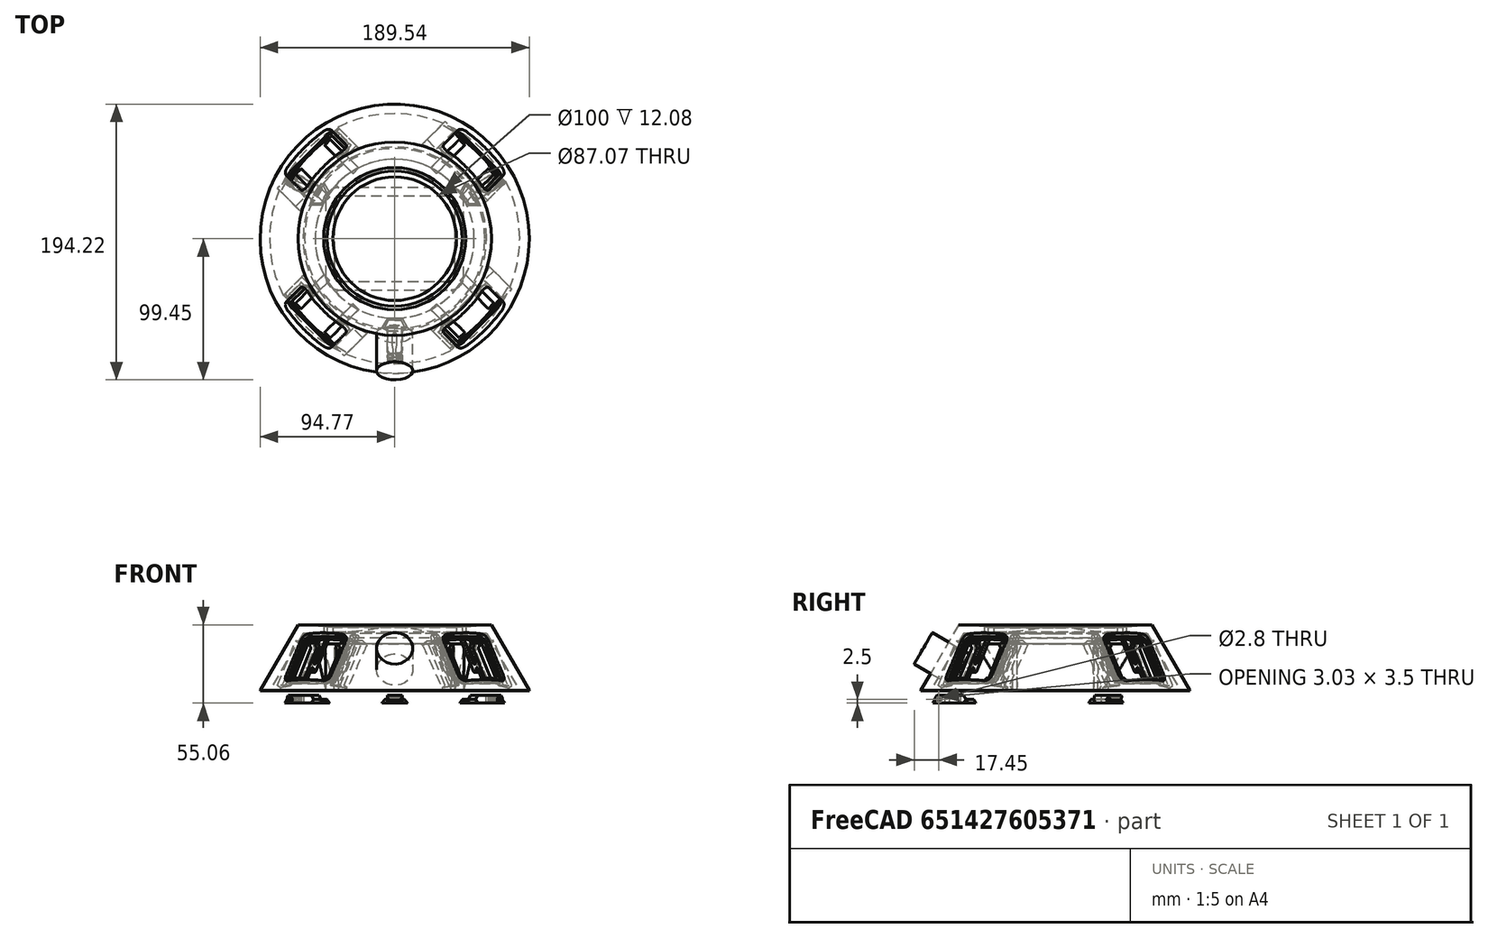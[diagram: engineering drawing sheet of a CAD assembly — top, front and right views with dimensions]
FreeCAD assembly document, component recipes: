
FREECAD ASSEMBLY — COMPONENT RECIPES ("case_v3_r2")

This assembly document has 20 components, labeled P0..P19 below (a component is one placed body or linked part). 20 of them carry a construction recipe — the FreeCAD feature program that regenerates the part from scratch, quoted from this document or its linked companion documents; the rest are supplied as boundary geometry only. No exploded tour is included for this assembly.
NOTE — this tour is split across 2 documents so each fits a 32k-token context. This is document 1: the component sections continue in the remaining 1 document, each repeating the header above.
COMPONENT P0 — recipe-attached ("BaseShape", modeled in this document).
Construction recipe (the document's own serialized feature program — sketch geometry with constraints, then the solid features built on it; lengths are millimeters unless a unit is written):

FEATURE [Sketcher::SketchObject] Sketch
  ArcFitTolerance = 1e-06
  AttachmentSupport = -> [XZ_Plane]
  FullyConstrained = true
  MakeInternals = false
  MapMode = 5
  Placement = pos=(0,0,0) rot=(1,0,0;1.5708rad)
  sketch-geometry (29):
    g0: LineSegment StartX=94.7691 StartY=0.4 StartZ=0 EndX=68.1243 EndY=46.55 EndZ=0
    g1: LineSegment [constr] StartX=50 StartY=45.0797 StartZ=0 EndX=50 EndY=0 EndZ=0
    g2: LineSegment [constr] StartX=50 StartY=0 StartZ=0 EndX=56 EndY=0 EndZ=0
    g3: LineSegment [constr] StartX=56 StartY=0 StartZ=0 EndX=56 EndY=33 EndZ=0
    g4: LineSegment StartX=63.55 StartY=40.55 StartZ=0 EndX=64.6602 EndY=40.55 EndZ=0
    g5: LineSegment StartX=64.6602 StartY=40.55 StartZ=0 EndX=88.0718 EndY=0 EndZ=0
    g6: LineSegment StartX=88.0718 StartY=0 StartZ=0 EndX=94.7681 EndY=0 EndZ=0
    g7: LineSegment StartX=50 StartY=45.0797 StartZ=0 EndX=68.1243 EndY=46.55 EndZ=0
    g8: LineSegment StartX=47.5346 StartY=44.8797 StartZ=0 EndX=43.5346 EndY=44.5552 EndZ=0
    g9: LineSegment StartX=47.5346 StartY=44.8797 StartZ=0 EndX=47.5346 EndY=37.3797 EndZ=0
    g10: LineSegment StartX=47.5346 StartY=37.3797 StartZ=0 EndX=0 EndY=37.3797 EndZ=0
    g11: LineSegment StartX=0 StartY=37.3797 StartZ=0 EndX=0 EndY=44.8797 EndZ=0
    g12: LineSegment StartX=43.5346 StartY=44.5552 StartZ=0 EndX=43.5346 EndY=41.3797 EndZ=0
    g13-g16: Circle [constr] x4 (B-spline internal-alignment scaffolding for g17; pole/knot coordinates omitted)
    g17: BSplineCurve PolesCount=4 KnotsCount=2 Degree=3 IsPeriodic=0
    g18: GeomPoint [constr] X=0 Y=44.8797 Z=0
    g19: GeomPoint [constr] X=43.5346 Y=41.3797 Z=0
    g20: GeomPoint [constr] X=95 Y=0 Z=0
    g21: ArcOfCircle [constr] CenterX=63.55 CenterY=33 CenterZ=0 NormalX=0 NormalY=0 NormalZ=1 AngleXU=0 Radius=7.55 StartAngle=1.5708 EndAngle=3.14159
    g22: GeomPoint [constr] X=56 Y=40.55 Z=0
    g23: LineSegment StartX=63.55 StartY=40.55 StartZ=0 EndX=56 EndY=33 EndZ=0
    g24: GeomPoint [constr] X=95 Y=0 Z=0
    g25: LineSegment StartX=94.7681 StartY=0 StartZ=0 EndX=94.7681 EndY=0.4 EndZ=0
    g26: LineSegment StartX=94.7691 StartY=0.4 StartZ=0 EndX=94.7681 EndY=0.4 EndZ=0
    g27: LineSegment StartX=56 StartY=33 StartZ=0 EndX=50 EndY=33 EndZ=0
    g28: LineSegment StartX=50 StartY=45.0797 StartZ=0 EndX=50 EndY=33 EndZ=0
  constraints (73):
    c: PointOnObject(g20,g-1)
    c: PointOnObject(g1,g-1)
    c: Coincident(g1,g2)
    c: PointOnObject(g2,g-1)
    c: Coincident(g2,g3)
    c: Horizontal(g4)
    c: Coincident(g4,g5)
    c: PointOnObject(g5,g-1)
    c: Coincident(g5,g6)
    c: DistanceX(g1) = 50
    c: Angle(g4,g5) = 2.0944
    c: Parallel(g5,g0)
    c: Distance(g20,g5) = 6
    c: Parallel(g3,g1)
    c: Distance(g1,g3) = 6
    c: Distance(g0,g4) = 6
    c: Vertical(g1)
    c: DistanceX(g20) = 95
    c: Coincident(g7,g1)
    c: Coincident(g7,g0)
    c: Distance(g22,g7) = 5
    c: Tangent(g8,g7)
    c: Coincident(g8,g9)
    c: Vertical(g9)
    c: Coincident(g9,g10)
    c: Horizontal(g10)
    c: Coincident(g10,g11)
    c: PointOnObject(g11,g-2)
    c: Vertical(g11)
    c: DistanceX(g8,g8) = 4
    c: Coincident(g12,g8)
    c: Vertical(g12)
    c: Weight(g13) = 1
    c: Equal(g13,g14)
    c: Equal(g13,g15)
    c: Equal(g13,g16)
    c: InternalAlignment(g13-g16 -> g17) x4
    c: InternalAlignment(g18,g17)
    c: InternalAlignment(g19,g17)
    c: Coincident(g17,g12)
    c: Coincident(g17,g11)
    c: Horizontal(g14,g11)
    c: Horizontal(g12,g15)
    c: DistanceY(g12,g11) = 3.5
    c: DistanceY(g10,g12) = 4
    c: Horizontal(g11,g8)
    c: Vertical(g15,g14)
    c: PointOnObject(g20,g0)
    c: PointOnObject(g20,g6)
    c: PointOnObject(g22,g3)
    c: PointOnObject(g22,g4)
    c: Tangent(g3,g21) = 1.5708
    c: Tangent(g4,g21) = 1.5708
    c: Coincident(g23,g3)
    c: Coincident(g23,g4)
    c: DistanceY(g0) = 46.55
    c: DistanceY(g8,g1) = 0.2
    c: DistanceY(g3) = 33
    c: PointOnObject(g24,g6)
    c: PointOnObject(g24,g0)
    c: Coincident(g25,g6)
    c: Vertical(g25)
    c: Coincident(g26,g0)
    c: Coincident(g26,g25)
    c: Horizontal(g26)
    c: DistanceY(g25,g25) = 0.4
    c: DistanceX(g26,g26) = 0.001
    c: DistanceX(g14) = 16
    c: Coincident(g27,g3)
    c: PointOnObject(g27,g1)
    c: Horizontal(g27)
    c: Coincident(g28,g1)
    c: Coincident(g28,g27)
FEATURE [PartDesign::Revolution] Revolution
  Angle = 360
  Angle2 = 60
  Axis = (0,2e-16,1)
  Base = (0,0,0)
  Placement = pos=(0,0,0) rot=(1,0,0;1.5708rad)
  Profile = -> Sketch
  ReferenceAxis = -> Sketch [V_Axis]
  Refine = true
  Suppressed = false
  Type = 0
FEATURE [PartDesign::SubShapeBinder] Binder012
  BindCopyOnChange = 0
  BindMode = 0
  ClaimChildren = false
  Context = -> Body [Binder012.]
  Fuse = false
  MakeFace = true
  OffsetFill = false
  OffsetIntersection = false
  OffsetJoinType = 0
  OffsetOpenResult = false
  PartialLoad = false
  Refine = true
  Relative = true
  Support = -> [Link001[Pad028.Face4]]
  _Version = 2
FEATURE [PartDesign::Pocket] Pocket  label="PocketDisplayBack"
  BaseFeature = -> Revolution
  Direction = (0.612372,0.612372,0.5)
  Length = 7
  Length2 = 1
  Placement = pos=(0,0,0) rot=(1,0,0;1.5708rad)
  Profile = -> Binder012
  Refine = true
  Reversed = true
  Suppressed = false
  Type = 4
FEATURE [PartDesign::PolarPattern] PolarPattern
  Angle = 360
  Axis = -> Z_Axis
  BaseFeature = -> Pocket
  Mode = 0
  Occurrences = 4
  Offset = 120
  Originals = -> [Pocket]
  Placement = pos=(0,0,0) rot=(1,0,0;1.5708rad)
  Refine = true
  Suppressed = false
  TransformMode = 0
FEATURE [PartDesign::Body] Body  label="BaseShape"
  AllowCompound = true
  Group = -> [Sketch,Revolution,Binder012,Pocket,PolarPattern]
  Origin = -> Origin
  Tip = -> PolarPattern
COMPONENT P1 — recipe-attached ("Bottom", modeled in this document).
Construction recipe (the document's own serialized feature program — sketch geometry with constraints, then the solid features built on it; lengths are millimeters unless a unit is written):

FEATURE [Sketcher::SketchObject] Sketch015
  ArcFitTolerance = 1e-06
  AttachmentSupport = -> [YZ_Plane010]
  FullyConstrained = true
  MakeInternals = false
  MapMode = 5
  Placement = pos=(0,0,0) rot=(0.57735,-0.57735,-0.57735;2.0944rad)
  sketch-geometry (27):
    g0: LineSegment StartX=94.7691 StartY=-1 StartZ=0 EndX=90.4389 EndY=-8.5 EndZ=0
    g1: LineSegment StartX=90.4389 StartY=-8.5 StartZ=0 EndX=10 EndY=-8.5 EndZ=0
    g2: LineSegment StartX=10 StartY=-8.5 StartZ=0 EndX=10 EndY=-2.5 EndZ=0
    g3: LineSegment StartX=94.1691 StartY=0 StartZ=0 EndX=94.1691 EndY=-0.6 EndZ=0
    g4: LineSegment StartX=94.7691 StartY=-0.6 StartZ=0 EndX=94.1691 EndY=-0.6 EndZ=0
    g5: LineSegment StartX=89.4876 StartY=-2.5 StartZ=0 EndX=10 EndY=-2.5 EndZ=0
    g6: LineSegment [constr] StartX=95 StartY=0 StartZ=0 EndX=89.2265 EndY=10 EndZ=0
    g7: LineSegment [constr] StartX=89 StartY=0 StartZ=0 EndX=83.2265 EndY=10 EndZ=0
    g8: LineSegment StartX=89.9876 StartY=1.1 StartZ=0 EndX=89.3876 EndY=1.7 EndZ=0
    g9: LineSegment StartX=89.3876 StartY=1.7 StartZ=0 EndX=89.9876 EndY=2.41505 EndZ=0
    g10: LineSegment StartX=89.9876 StartY=2.41505 StartZ=0 EndX=91.7876 EndY=2.41505 EndZ=0
    g11: LineSegment StartX=92.6876 StartY=1.7 StartZ=0 EndX=92.2876 EndY=1.7 EndZ=0
    g12: LineSegment [constr] StartX=92.6876 StartY=1.7 StartZ=0 EndX=93.6691 EndY=0 EndZ=0
    g13: LineSegment StartX=94.7691 StartY=-0.6 StartZ=0 EndX=94.7691 EndY=-1 EndZ=0
    g14: LineSegment [constr] StartX=94.7691 StartY=-1 StartZ=0 EndX=95 EndY=-0.6 EndZ=0
    g15: LineSegment [constr] StartX=95 StartY=-0.6 StartZ=0 EndX=94.7691 EndY=-0.6 EndZ=0
    g16: LineSegment StartX=94.1691 StartY=0 StartZ=0 EndX=92.6876 EndY=0 EndZ=0
    g17: LineSegment StartX=89.9876 StartY=1.1 StartZ=0 EndX=89.9876 EndY=0 EndZ=0
    g18: LineSegment StartX=89.9876 StartY=0 StartZ=0 EndX=89.9876 EndY=-3.9 EndZ=0
    g19: LineSegment StartX=91.7876 StartY=-2.9 StartZ=0 EndX=91.7876 EndY=0 EndZ=0
    g20: LineSegment StartX=91.7876 StartY=0 StartZ=0 EndX=91.7876 EndY=2.41505 EndZ=0
    g21: LineSegment StartX=92.2876 StartY=1.7 StartZ=0 EndX=92.2876 EndY=0 EndZ=0
    g22: LineSegment StartX=92.2876 StartY=0 StartZ=0 EndX=92.2876 EndY=-2.9 EndZ=0
    g23: LineSegment StartX=91.7876 StartY=-2.9 StartZ=0 EndX=92.2876 EndY=-2.9 EndZ=0
    g24: LineSegment StartX=89.4876 StartY=-2.5 StartZ=0 EndX=89.4876 EndY=-3.9 EndZ=0
    g25: LineSegment StartX=89.4876 StartY=-3.9 StartZ=0 EndX=89.9876 EndY=-3.9 EndZ=0
    g26: LineSegment StartX=92.6876 StartY=0 StartZ=0 EndX=92.6876 EndY=1.7 EndZ=0
  constraints (81):
    c: Coincident(g0,g1)
    c: Horizontal(g1)
    c: Coincident(g1,g2)
    c: Vertical(g2)
    c: Angle(g0,g1) = 2.0944
    c: DistanceX(g2) = 10
    c: Coincident(g4,g3)
    c: Horizontal(g4)
    c: DistanceX(g4,g4) = 0.6
    c: Horizontal(g5)
    c: Coincident(g2,g5)
    c: Vertical(g3)
    c: PointOnObject(g6,g-1)
    c: Angle(g-1,g6) = 2.0944
    c: PointOnObject(g7,g-1)
    c: DistanceX(g7) = 89
    c: Parallel(g7,g6)
    c: DistanceY(g0) = -8.5
    c: Coincident(g8,g9)
    c: Coincident(g9,g10)
    c: Horizontal(g10)
    c: DistanceX(g8,g8) = 0.6
    c: Angle(g9,g10) = 2.26893
    c: Distance(g12,g3) = 0.5
    c: DistanceX(g10,g10) = 1.8
    c: Angle(g12,g-1) = 1.0472
    c: Coincident(g12,g11)
    c: Horizontal(g6,g7)
    c: DistanceY(g7) = 10
    c: DistanceY(g8) = 1.7
    c: Coincident(g13,g4)
    c: Vertical(g13)
    c: DistanceY(g13,g13) = 0.4
    c: Coincident(g14,g15)
    c: Coincident(g15,g4)
    c: Horizontal(g15)
    c: Tangent(g0,g14) = 1.5708
    c: DistanceX(g14) = 95
    c: Coincident(g0,g13)
    c: Vertical(g6,g14)
    c: DistanceY(g4) = -0.6
    c: Coincident(g16,g3)
    c: Horizontal(g16)
    c: PointOnObject(g12,g16)
    c: DistanceY(g5) = -2.5
    c: Horizontal(g8,g11)
    c: DistanceX(g8,g11) = 3.3
    c: Angle(g8,g-1) = 0.785398
    c: Coincident(g8,g17)
    c: PointOnObject(g17,g-1)
    c: Vertical(g17)
    c: Coincident(g17,g18)
    c: PointOnObject(g19,g-1)
    c: Coincident(g19,g20)
    c: Coincident(g20,g10)
    c: Vertical(g20)
    c: PointOnObject(g21,g-1)
    c: Coincident(g21,g22)
    c: PointOnObject(g16,g-1)
    c: Vertical(g21)
    c: Coincident(g23,g19)
    c: Coincident(g23,g22)
    c: Parallel(g19,g18)
    c: Coincident(g5,g24)
    c: Coincident(g24,g25)
    c: Coincident(g25,g18)
    c: Horizontal(g25)
    c: Horizontal(g23)
    c: Parallel(g19,g22)
    c: Parallel(g24,g18)
    c: Coincident(g26,g11)
    c: Vertical(g26)
    c: DistanceY(g18,g8) = 5
    c: Vertical(g18)
    c: Coincident(g26,g16)
    c: Vertical(g8,g9)
    c: Coincident(g21,g11)
    c: DistanceX(g10,g11) = 0.5
    c: Horizontal(g11)
    c: Equal(g23,g25)
    c: DistanceY(g18,g19) = 1
FEATURE [PartDesign::Revolution] Revolution001
  Angle = 360
  Angle2 = 60
  Axis = (0,0,1)
  Base = (0,0,0)
  Placement = pos=(0,0,0) rot=(1,1,1;2.0944rad)
  Profile = -> Sketch015
  ReferenceAxis = -> Sketch015 [V_Axis]
  Refine = true
  Reversed = true
  Suppressed = false
  Type = 0
FEATURE [Sketcher::SketchObject] Sketch021
  ArcFitTolerance = 1e-06
  AttachmentOffset = pos=(0,0,0) rot=(0,0,1;-1.5708rad)
  AttachmentSupport = -> [XY_Plane010]
  FullyConstrained = true
  MakeInternals = false
  MapMode = 5
  Placement = pos=(0,0,0) rot=(0,0,1;4.71239rad)
  sketch-geometry (4):
    g0: LineSegment StartX=-97.6 StartY=7.575 StartZ=0 EndX=-97.6 EndY=-7.575 EndZ=0
    g1: LineSegment StartX=-97.6 StartY=-7.575 StartZ=0 EndX=-86.8 EndY=-7.575 EndZ=0
    g2: LineSegment StartX=-86.8 StartY=-7.575 StartZ=0 EndX=-86.8 EndY=7.575 EndZ=0
    g3: LineSegment StartX=-86.8 StartY=7.575 StartZ=0 EndX=-97.6 EndY=7.575 EndZ=0
  constraints (11):
    c: Coincident(g0,g1)
    c: Coincident(g1,g2)
    c: Coincident(g2,g3)
    c: Coincident(g3,g0)
    c: Vertical(g0)
    c: Horizontal(g1)
    c: Horizontal(g3)
    c: Symmetric(g2,g1,g-1)
    c: DistanceY(g0,g0) = 15.15
    c: DistanceX(g1,g1) = 10.8
    c: DistanceX(g1) = -86.8
FEATURE [Sketcher::SketchObject] Sketch037
  ArcFitTolerance = 1e-06
  AttachmentOffset = pos=(0,0,0) rot=(0,0,1;-1.5708rad)
  AttachmentSupport = -> [XY_Plane010]
  FullyConstrained = true
  MakeInternals = false
  MapMode = 5
  Placement = pos=(0,0,0) rot=(0,0,1;4.71239rad)
  sketch-geometry (18):
    g0: LineSegment StartX=-30 StartY=39.5 StartZ=0 EndX=-30 EndY=-39.5 EndZ=0
    g1: LineSegment StartX=-27 StartY=-42.5 StartZ=0 EndX=27 EndY=-42.5 EndZ=0
    g2: LineSegment StartX=30 StartY=-39.5 StartZ=0 EndX=30 EndY=39.5 EndZ=0
    g3: LineSegment StartX=27 StartY=42.5 StartZ=0 EndX=11 EndY=42.5 EndZ=0
    g4: ArcOfCircle CenterX=-27 CenterY=39.5 CenterZ=0 NormalX=0 NormalY=0 NormalZ=1 AngleXU=0 Radius=3 StartAngle=1.5708 EndAngle=3.14159
    g5: ArcOfCircle CenterX=-27 CenterY=-39.5 CenterZ=0 NormalX=0 NormalY=0 NormalZ=1 AngleXU=0 Radius=3 StartAngle=3.14159 EndAngle=4.71239
    g6: ArcOfCircle CenterX=27 CenterY=-39.5 CenterZ=0 NormalX=0 NormalY=0 NormalZ=1 AngleXU=0 Radius=3 StartAngle=4.71239 EndAngle=6.28319
    g7: ArcOfCircle CenterX=27 CenterY=39.5 CenterZ=0 NormalX=0 NormalY=0 NormalZ=1 AngleXU=0 Radius=3 StartAngle=-9e-16 EndAngle=1.5708
    g8: GeomPoint [constr] X=30 Y=-42.5 Z=0
    g9: GeomPoint [constr] X=0 Y=0 Z=0
    g10: LineSegment StartX=-6 StartY=47.5 StartZ=0 EndX=-6 EndY=62.5 EndZ=0
    g11: ArcOfCircle CenterX=-3 CenterY=62.5 CenterZ=0 NormalX=0 NormalY=0 NormalZ=1 AngleXU=0 Radius=3 StartAngle=1.5708 EndAngle=3.14159
    g12: LineSegment StartX=-3 StartY=65.5 StartZ=0 EndX=3 EndY=65.5 EndZ=0
    g13: ArcOfCircle CenterX=3 CenterY=62.5 CenterZ=0 NormalX=0 NormalY=0 NormalZ=1 AngleXU=0 Radius=3 StartAngle=1.1e-15 EndAngle=1.5708
    g14: LineSegment StartX=6 StartY=62.5 StartZ=0 EndX=6 EndY=47.5 EndZ=0
    g15: ArcOfCircle CenterX=11 CenterY=47.5 CenterZ=0 NormalX=0 NormalY=0 NormalZ=1 AngleXU=0 Radius=5 StartAngle=3.14159 EndAngle=4.71239
    g16: LineSegment StartX=-11 StartY=42.5 StartZ=0 EndX=-27 EndY=42.5 EndZ=0
    g17: ArcOfCircle CenterX=-11 CenterY=47.5 CenterZ=0 NormalX=0 NormalY=0 NormalZ=1 AngleXU=0 Radius=5 StartAngle=4.71239 EndAngle=6.28319
  constraints (42):
    c: Tangent(g0,g4) = -1.5708
    c: Tangent(g0,g5) = -1.5708
    c: Tangent(g1,g5) = -1.5708
    c: Tangent(g1,g6) = -1.5708
    c: Tangent(g2,g6) = -1.5708
    c: Tangent(g2,g7) = -1.5708
    c: Tangent(g3,g7) = -1.5708
    c: Vertical(g0)
    c: Vertical(g2)
    c: Horizontal(g1)
    c: Horizontal(g3)
    c: Equal(g4,g5)
    c: Equal(g5,g6)
    c: Equal(g6,g7)
    c: Symmetric(g2,g0,g9)
    c: PointOnObject(g8,g1)
    c: PointOnObject(g8,g2)
    c: Coincident(g9,g-1)
    c: Radius(g6) = 3
    c: DistanceY(g1,g16) = 85
    c: DistanceX(g0,g2) = 60
    c: Vertical(g10)
    c: Tangent(g10,g11) = 1.5708
    c: Tangent(g11,g12) = 1.5708
    c: Tangent(g12,g13) = 1.5708
    c: Tangent(g13,g14) = 1.5708
    c: Tangent(g14,g15) = -1.5708
    c: Tangent(g10,g17) = -1.5708
    c: Vertical(g14)
    c: Horizontal(g12)
    c: Equal(g11,g13)
    c: Tangent(g3,g15) = 1.5708
    c: Horizontal(g3,g16)
    c: Horizontal(g16)
    c: DistanceX(g10,g13) = 12
    c: Equal(g16,g3)
    c: DistanceY(g14,g14) = 15
    c: Tangent(g17,g16) = 1.5708
    c: Tangent(g16,g4) = -1.5708
    c: Equal(g15,g17)
    c: Radius(g17) = 5
    c: Equal(g13,g7)
FEATURE [Sketcher::SketchObject] Sketch038
  ArcFitTolerance = 1e-06
  AttachmentSupport = -> [XY_Plane010]
  FullyConstrained = true
  MakeInternals = false
  MapMode = 5
  sketch-geometry (5):
    g0: LineSegment StartX=-20 StartY=85.5 StartZ=0 EndX=-20 EndY=65.5 EndZ=0
    g1: LineSegment StartX=-20 StartY=65.5 StartZ=0 EndX=20 EndY=65.5 EndZ=0
    g2: LineSegment StartX=20 StartY=65.5 StartZ=0 EndX=20 EndY=85.5 EndZ=0
    g3: LineSegment StartX=20 StartY=85.5 StartZ=0 EndX=-20 EndY=85.5 EndZ=0
    g4: GeomPoint [constr] X=0 Y=75.5 Z=0
  constraints (13):
    c: Coincident(g0,g1)
    c: Coincident(g1,g2)
    c: Coincident(g2,g3)
    c: Coincident(g3,g0)
    c: Vertical(g0)
    c: Vertical(g2)
    c: Horizontal(g1)
    c: Horizontal(g3)
    c: Symmetric(g2,g0,g4)
    c: PointOnObject(g4,g-2)
    c: DistanceY(g2) = 85.5
    c: DistanceY(g2,g2) = 20
    c: DistanceX(g1,g1) = 40
FEATURE [Sketcher::SketchObject] Sketch040
  ArcFitTolerance = 1e-06
  AttachmentSupport = -> [YZ_Plane010]
  FullyConstrained = true
  MakeInternals = false
  MapMode = 5
  Placement = pos=(0,0,0) rot=(0.57735,0.57735,0.57735;2.0944rad)
  sketch-geometry (4):
    g0: LineSegment StartX=-32 StartY=-0.1 StartZ=0 EndX=-32.5 EndY=0.766025 EndZ=0
    g1: LineSegment StartX=-32.5 StartY=0.766025 StartZ=0 EndX=-33.5 EndY=0.766025 EndZ=0
    g2: LineSegment StartX=-33.5 StartY=0.766025 StartZ=0 EndX=-34 EndY=-0.1 EndZ=0
    g3: LineSegment StartX=-34 StartY=-0.1 StartZ=0 EndX=-32 EndY=-0.1 EndZ=0
  constraints (12):
    c: Coincident(g0,g1)
    c: Horizontal(g1)
    c: Coincident(g1,g2)
    c: Coincident(g2,g3)
    c: Coincident(g3,g0)
    c: Horizontal(g3)
    c: Angle(g2,g1) = 2.0944
    c: Angle(g1,g0) = 2.0944
    c: DistanceX(g3,g3) = 2
    c: DistanceX(g1,g1) = 1
    c: DistanceX(g0) = -32
    c: DistanceY(g2) = -0.1
FEATURE [Sketcher::SketchObject] Sketch054
  ArcFitTolerance = 1e-06
  AttachmentOffset = pos=(0,0,8.5) rot=(0,0,1;0rad)
  AttachmentSupport = -> [XY_Plane010]
  FullyConstrained = true
  MakeInternals = false
  MapMode = 5
  Placement = pos=(0,0,-8.5) rot=(0,1,0;3.14159rad)
  sketch-geometry (4):
    g0: Circle CenterX=-42 CenterY=38.5 CenterZ=0 NormalX=0 NormalY=0 NormalZ=1 AngleXU=0 Radius=4.75
    g1: Circle CenterX=42 CenterY=38.5 CenterZ=0 NormalX=0 NormalY=0 NormalZ=1 AngleXU=0 Radius=4.75
    g2: Circle CenterX=42 CenterY=-38.5 CenterZ=0 NormalX=0 NormalY=0 NormalZ=1 AngleXU=0 Radius=4.75
    g3: Circle CenterX=-42 CenterY=-38.5 CenterZ=0 NormalX=0 NormalY=0 NormalZ=1 AngleXU=0 Radius=4.75
  constraints (11):
    c: Horizontal(g3,g2)
    c: Horizontal(g1,g0)
    c: Vertical(g0,g3)
    c: Vertical(g1,g2)
    c: Symmetric(g0,g2,g-1)
    c: DistanceX(g3,g2) = 84
    c: DistanceY(g2,g1) = 77
    c: Equal(g0,g1)
    c: Equal(g1,g2)
    c: Equal(g2,g3)
    c: Diameter(g3) = 9.5
FEATURE [Sketcher::SketchObject] Sketch073
  ArcFitTolerance = 1e-06
  AttachmentSupport = -> [XY_Plane010]
  FullyConstrained = true
  MakeInternals = false
  MapMode = 5
  sketch-geometry (5):
    g0: LineSegment StartX=-11.5 StartY=93.25 StartZ=0 EndX=-11.5 EndY=85.75 EndZ=0
    g1: LineSegment StartX=-11.5 StartY=85.75 StartZ=0 EndX=11.5 EndY=85.75 EndZ=0
    g2: LineSegment StartX=11.5 StartY=85.75 StartZ=0 EndX=11.5 EndY=93.25 EndZ=0
    g3: LineSegment StartX=11.5 StartY=93.25 StartZ=0 EndX=-11.5 EndY=93.25 EndZ=0
    g4: GeomPoint [constr] X=0 Y=89.5 Z=0
  constraints (13):
    c: Coincident(g0,g1)
    c: Coincident(g1,g2)
    c: Coincident(g2,g3)
    c: Coincident(g3,g0)
    c: Vertical(g0)
    c: Vertical(g2)
    c: Horizontal(g1)
    c: Horizontal(g3)
    c: Symmetric(g2,g0,g4)
    c: PointOnObject(g4,g-2)
    c: DistanceX(g3,g3) = 23
    c: DistanceY(g2,g2) = 7.5
    c: DistanceY(g4) = 89.5
FEATURE [Sketcher::SketchObject] Sketch074
  ArcFitTolerance = 1e-06
  AttachmentSupport = -> [XY_Plane010]
  FullyConstrained = true
  MakeInternals = false
  MapMode = 5
  sketch-geometry (5):
    g0: LineSegment StartX=-12.5 StartY=87.5 StartZ=0 EndX=12.5 EndY=87.5 EndZ=0
    g1: LineSegment StartX=12.5 StartY=87.5 StartZ=0 EndX=12.5 EndY=92.5 EndZ=0
    g2: LineSegment StartX=12.5 StartY=92.5 StartZ=0 EndX=-12.5 EndY=92.5 EndZ=0
    g3: LineSegment StartX=-12.5 StartY=92.5 StartZ=0 EndX=-12.5 EndY=87.5 EndZ=0
    g4: GeomPoint [constr] X=0 Y=90 Z=0
  constraints (13):
    c: Coincident(g0,g1)
    c: Coincident(g1,g2)
    c: Coincident(g2,g3)
    c: Coincident(g3,g0)
    c: Horizontal(g0)
    c: Horizontal(g2)
    c: Vertical(g1)
    c: Vertical(g3)
    c: Symmetric(g2,g0,g4)
    c: Distance(g1,g3) = 25
    c: Distance(g0,g2) = 5
    c: PointOnObject(g4,g-2)
    c: DistanceY(g4) = 90
FEATURE [PartDesign::SubShapeBinder] Binder045
  BindCopyOnChange = 0
  BindMode = 0
  ClaimChildren = false
  Context = -> Body010 [Binder045.]
  Fuse = false
  MakeFace = true
  Offset = 6
  OffsetFill = true
  OffsetIntersection = false
  OffsetJoinType = 1
  OffsetOpenResult = false
  PartialLoad = false
  Placement = pos=(0,0,-0.1) rot=(0,0,1;0rad)
  Refine = true
  Relative = true
  Support = -> [Sketch037]
  _Version = 2
FEATURE [PartDesign::SubShapeBinder] Binder046
  BindCopyOnChange = 0
  BindMode = 0
  ClaimChildren = false
  Context = -> Body010 [Binder046.]
  Fuse = false
  MakeFace = true
  OffsetFill = false
  OffsetIntersection = false
  OffsetJoinType = 0
  OffsetOpenResult = false
  PartialLoad = false
  Refine = true
  Relative = true
  Support = -> [Sketch054]
  _Version = 2
FEATURE [PartDesign::SubShapeBinder] Binder047  label="BinderUsb"
  BindCopyOnChange = 0
  BindMode = 0
  ClaimChildren = false
  Context = -> Body010 [Binder047.]
  Fuse = false
  MakeFace = true
  Offset = 0.15
  OffsetFill = false
  OffsetIntersection = false
  OffsetJoinType = 1
  OffsetOpenResult = false
  PartialLoad = false
  Placement = pos=(0,0,0.6) rot=(0,0,1;0rad)
  Refine = true
  Relative = true
  Support = -> [Boolean010[Face308]]
  _Version = 2
FEATURE [PartDesign::SubShapeBinder] Binder049
  BindCopyOnChange = 0
  BindMode = 0
  ClaimChildren = false
  Context = -> Body010 [Binder049.]
  Fuse = false
  MakeFace = true
  Offset = 0.1
  OffsetFill = false
  OffsetIntersection = false
  OffsetJoinType = 0
  OffsetOpenResult = false
  PartialLoad = false
  Refine = true
  Relative = true
  Support = -> [Pocket015[Face324]]
  _Version = 2
FEATURE [Sketcher::SketchObject] Sketch081
  ArcFitTolerance = 1e-06
  AttachmentOffset = pos=(0,0,-8.5) rot=(0,0,1;0rad)
  AttachmentSupport = -> [XY_Plane010]
  FullyConstrained = true
  MakeInternals = false
  MapMode = 5
  Placement = pos=(0,0,-8.5) rot=(0,0,1;0rad)
  sketch-geometry (13):
    g0: Circle CenterX=-40.5 CenterY=-70.1481 CenterZ=0 NormalX=0 NormalY=0 NormalZ=1 AngleXU=0 Radius=4
    g1: LineSegment [constr] StartX=40.5 StartY=-70.1481 StartZ=0 EndX=81 EndY=-1.42e-14 EndZ=0
    g2: LineSegment [constr] StartX=81 StartY=-1.42e-14 StartZ=0 EndX=40.5 EndY=70.1481 EndZ=0
    g3: LineSegment [constr] StartX=40.5 StartY=70.1481 StartZ=0 EndX=-40.5 EndY=70.1481 EndZ=0
    g4: LineSegment [constr] StartX=-40.5 StartY=70.1481 StartZ=0 EndX=-81 EndY=4.26e-14 EndZ=0
    g5: LineSegment [constr] StartX=-81 StartY=4.26e-14 StartZ=0 EndX=-40.5 EndY=-70.1481 EndZ=0
    g6: LineSegment [constr] StartX=-40.5 StartY=-70.1481 StartZ=0 EndX=40.5 EndY=-70.1481 EndZ=0
    g7: Circle [constr] CenterX=0 CenterY=0 CenterZ=0 NormalX=0 NormalY=0 NormalZ=1 AngleXU=0 Radius=81
    g8: Circle CenterX=40.5 CenterY=-70.1481 CenterZ=0 NormalX=0 NormalY=0 NormalZ=1 AngleXU=0 Radius=4
    g9: Circle CenterX=81 CenterY=-1.42e-14 CenterZ=0 NormalX=0 NormalY=0 NormalZ=1 AngleXU=0 Radius=4
    g10: Circle CenterX=-81 CenterY=4.26e-14 CenterZ=0 NormalX=0 NormalY=0 NormalZ=1 AngleXU=0 Radius=4
    g11: Circle CenterX=-40.5 CenterY=70.1481 CenterZ=0 NormalX=0 NormalY=0 NormalZ=1 AngleXU=0 Radius=4
    g12: Circle CenterX=40.5 CenterY=70.1481 CenterZ=0 NormalX=0 NormalY=0 NormalZ=1 AngleXU=0 Radius=4
  constraints (28):
    c: Diameter(g0) = 8
    c: Coincident(g1,g2)
    c: Coincident(g2,g3)
    c: Coincident(g3,g4)
    c: Coincident(g4,g5)
    c: Coincident(g5,g6)
    c: Coincident(g6,g1)
    c: Equal(g1, g2-g6) x5
    c: PointOnObject(g1,g7)
    c: PointOnObject(g2,g7)
    c: PointOnObject(g3,g7)
    c: PointOnObject(g4,g7)
    c: PointOnObject(g5,g7)
    c: PointOnObject(g6,g7)
    c: Coincident(g7,g-1)
    c: Horizontal(g6)
    c: Coincident(g0,g5)
    c: Coincident(g8,g1)
    c: Coincident(g9,g1)
    c: Coincident(g10,g4)
    c: Coincident(g11,g3)
    c: Coincident(g12,g2)
    c: Equal(g12,g11)
    c: Equal(g11,g10)
    c: Equal(g10,g9)
    c: Equal(g9,g8)
    c: Equal(g8,g0)
    c: Diameter(g7) = 162
FEATURE [PartDesign::SubShapeBinder] Binder056  label="BinderBoard"
  BindCopyOnChange = 0
  BindMode = 0
  ClaimChildren = false
  Context = -> Body010 [Binder056.]
  Fuse = false
  MakeFace = true
  OffsetFill = false
  OffsetIntersection = false
  OffsetJoinType = 1
  OffsetOpenResult = false
  PartialLoad = false
  Refine = true
  Relative = true
  Support = -> [Boolean010[Face305]]
  _Version = 2
FEATURE [Sketcher::SketchObject] Sketch088
  ArcFitTolerance = 1e-06
  AttachmentSupport = -> [YZ_Plane010]
  FullyConstrained = true
  MakeInternals = false
  MapMode = 5
  Placement = pos=(0,0,0) rot=(0.57735,0.57735,0.57735;2.0944rad)
  sketch-geometry (4):
    g0: LineSegment StartX=-92.1 StartY=3 StartZ=0 EndX=-92.1 EndY=-2 EndZ=0
    g1: LineSegment StartX=-92.1 StartY=-2 StartZ=0 EndX=-89.1 EndY=-2 EndZ=0
    g2: LineSegment StartX=-89.1 StartY=-2 StartZ=0 EndX=-89.1 EndY=3 EndZ=0
    g3: LineSegment StartX=-89.1 StartY=3 StartZ=0 EndX=-92.1 EndY=3 EndZ=0
  constraints (12):
    c: Coincident(g0,g1)
    c: Coincident(g1,g2)
    c: Coincident(g2,g3)
    c: Coincident(g3,g0)
    c: Vertical(g0)
    c: Vertical(g2)
    c: Horizontal(g1)
    c: Horizontal(g3)
    c: DistanceY(g1) = -2
    c: DistanceY(g2,g2) = 5
    c: DistanceX(g0) = -92.1
    c: DistanceX(g1,g1) = 3
FEATURE [PartDesign::Groove] Groove002
  Angle = 2
  Angle2 = 60
  Axis = (0,0,1)
  Base = (0,0,0)
  BaseFeature = -> Revolution001
  Midplane = true
  Placement = pos=(0,0,0) rot=(1,1,1;2.0944rad)
  Profile = -> Sketch088
  ReferenceAxis = -> Sketch088 [V_Axis]
  Refine = true
  Reversed = true
  Suppressed = false
  Type = 0
FEATURE [PartDesign::PolarPattern] PolarPattern016
  Angle = 360
  Axis = -> Z_Axis010
  BaseFeature = -> Groove002
  Mode = 0
  Occurrences = 36
  Offset = 120
  Originals = -> [Groove002]
  Placement = pos=(0,0,0) rot=(1,1,1;2.0944rad)
  Refine = true
  Suppressed = false
  TransformMode = 0
FEATURE [PartDesign::Pad] Pad030  label="PadUSB"
  BaseFeature = -> PolarPattern016
  Direction = (0,0.32,1)
  Length = 5
  Length2 = 10
  Placement = pos=(0,0,0) rot=(1,1,1;2.0944rad)
  Profile = -> Sketch073
  ReferenceAxis = -> Sketch073 [N_Axis]
  Refine = true
  Reversed = true
  Suppressed = false
  Type = 0
  UseCustomVector = true
FEATURE [PartDesign::Boolean] Boolean  label="BooleanUSB002"
  BaseFeature = -> Pad030
  Group = -> [Binder]
  Refine = true
  Suppressed = false
  Type = 1
  UsePlacement = true
FEATURE [PartDesign::Pocket] Pocket001  label="PocketUSB"
  BaseFeature = -> Boolean
  Direction = (0,0,-1)
  Length = 10
  Length2 = 5
  Profile = -> Sketch021
  ReferenceAxis = -> Sketch021 [N_Axis]
  Refine = true
  Suppressed = false
  Type = 4
FEATURE [PartDesign::Pocket] Pocket013  label="PocketUSB2"
  BaseFeature = -> Pocket001
  Direction = (0,0,-1)
  Length = 5
  Length2 = 5
  Profile = -> Sketch074
  ReferenceAxis = -> Sketch074 [N_Axis]
  Refine = true
  Reversed = true
  Suppressed = false
  Type = 0
FEATURE [PartDesign::Boolean] Boolean001  label="BooleanAkku001"
  BaseFeature = -> Pocket013
  Group = -> [Binder015]
  Refine = true
  Suppressed = false
  Type = 1
  UsePlacement = true
FEATURE [PartDesign::Pad] Pad031
  BaseFeature = -> Boolean001
  Direction = (0,0,1)
  Length = 5
  Length2 = 10
  Profile = -> Binder045
  Refine = true
  Reversed = true
  Suppressed = false
  Type = 0
FEATURE [PartDesign::Pocket] Pocket004  label="PocketInner"
  BaseFeature = -> Pad031
  Direction = (0,0,-1)
  Length = 9
  Length2 = 5
  Profile = -> Sketch037
  ReferenceAxis = -> Sketch037 [N_Axis]
  Refine = true
  Suppressed = false
  TaperAngle = 20
  Type = 0
FEATURE [PartDesign::AdditivePipe] AdditivePipe
  AuxilleryCurvelinear = true
  AuxillerySpineTangent = false
  BaseFeature = -> Pocket004
  Binormal = (0,0,0)
  Mode = 0
  Profile = -> Sketch040
  Refine = true
  Spine = -> Sketch037
  SpineTangent = false
  Suppressed = false
  Transformation = 0
  Transition = 0
FEATURE [PartDesign::Boolean] Boolean010  label="BooleanEsp"
  BaseFeature = -> AdditivePipe
  Group = -> [Binder029]
  Refine = true
  Suppressed = false
  Type = 1
  UsePlacement = true
FEATURE [PartDesign::Pocket] Pocket015  label="PocketESPBoard"
  BaseFeature = -> Boolean010
  Direction = (-1.68587e-07,-1.04308e-07,-1)
  Length = 14
  Length2 = 5
  Profile = -> Binder056
  Refine = true
  Reversed = true
  Suppressed = false
  TaperAngle = 20
  Type = 0
FEATURE [PartDesign::Pocket] Pocket014  label="PocketESPUSB"
  BaseFeature = -> Pocket015
  Direction = (1.68587e-07,1.04308e-07,1)
  Length = 7
  Length2 = 5
  Profile = -> Binder047
  Refine = true
  Suppressed = false
  TaperAngle = 19
  Type = 4
FEATURE [PartDesign::Pocket] Pocket005  label="PocketCables"
  BaseFeature = -> Pocket014
  Direction = (0,0,-1)
  Length = 4
  Length2 = 5
  Profile = -> Sketch038
  ReferenceAxis = -> Sketch038 [N_Axis]
  Refine = true
  Suppressed = false
  TaperAngle = -45
  Type = 0
FEATURE [PartDesign::Pad] Pad032
  BaseFeature = -> Pocket005
  Direction = (0,0,1)
  Length = 8.4
  Length2 = 10
  Profile = -> Binder046
  Refine = true
  Suppressed = false
  Type = 0
FEATURE [PartDesign::Hole] Hole
  BaseFeature = -> Pad032
  CustomThreadClearance = 0
  Depth = 25
  DepthType = 0
  Diameter = 4.5
  DrillForDepth = false
  DrillPoint = 1
  DrillPointAngle = 118
  HoleCutCountersinkAngle = 90
  HoleCutCustomValues = false
  HoleCutDepth = 4.4
  HoleCutDiameter = 8
  HoleCutType = 1
  ModelThread = false
  Profile = -> Sketch054
  Refine = true
  Suppressed = false
  Tapered = false
  TaperedAngle = 90
  ThreadClass = 0
  ThreadDepth = 25
  ThreadDepthType = 0
  ThreadDirection = 0
  ThreadFit = 0
  ThreadSize = 11
  ThreadType = 1
  Threaded = false
  UseCustomThreadClearance = false
FEATURE [PartDesign::Pocket] Pocket018
  BaseFeature = -> Hole
  Direction = (0,0,-1)
  Length = 3.5
  Length2 = 5
  Profile = -> Sketch081
  ReferenceAxis = -> Sketch081 [N_Axis]
  Refine = true
  Reversed = true
  Suppressed = true
  Type = 0
FEATURE [PartDesign::Boolean] Boolean021  label="BooleanFeet"
  BaseFeature = -> Pocket018
  Group = -> [Binder054]
  Refine = true
  Suppressed = false
  Type = 1
  UsePlacement = true
FEATURE [PartDesign::Boolean] Boolean022  label="BooleanPattern"
  BaseFeature = -> Boolean021
  Group = -> [Binder055]
  Refine = true
  Suppressed = false
  Type = 1
  UsePlacement = true
FEATURE [PartDesign::Body] Body010  label="Bottom"
  AllowCompound = true
  Group = -> [Sketch015,Revolution001,Sketch021,Sketch073,Sketch088,Groove002,PolarPattern016,Pad030,Boolean,Pocket001,Sketch074,Pocket013,Boolean001,Sketch037,Pad031,Pocket004,Binder045,AdditivePipe,Boolean010,Sketch038,Binder047,Binder056,Pocket015,Pocket014,Binder049,Pocket005,Sketch040,Sketch054,Binder046,Pad032,Hole,Sketch081,Pocket018,Boolean021,Boolean022]
  Origin = -> Origin010
  Tip = -> Boolean022
COMPONENT P2 — recipe-attached ("Button", modeled in this document).
Construction recipe (the document's own serialized feature program — sketch geometry with constraints, then the solid features built on it; lengths are millimeters unless a unit is written):

FEATURE [Sketcher::SketchObject] Sketch017
  ArcFitTolerance = 1e-06
  AttachmentSupport = -> [XY_Plane011]
  FullyConstrained = true
  MakeInternals = false
  MapMode = 5
  sketch-geometry (7):
    g0: LineSegment StartX=0 StartY=3 StartZ=0 EndX=8 EndY=3 EndZ=0
    g1: LineSegment StartX=8 StartY=3 StartZ=0 EndX=8 EndY=0 EndZ=0
    g2: LineSegment StartX=8 StartY=0 StartZ=0 EndX=9 EndY=-1.1e-15 EndZ=0
    g3: ArcOfCircle CenterX=27.5 CenterY=-3.4e-15 CenterZ=0 NormalX=0 NormalY=0 NormalZ=1 AngleXU=0 Radius=18.5 StartAngle=2.8113 EndAngle=3.14159
    g4: ArcOfCircle CenterX=-7.5 CenterY=12 CenterZ=0 NormalX=0 NormalY=0 NormalZ=1 AngleXU=0 Radius=18.5 StartAngle=5.95289 EndAngle=6.28319
    g5: LineSegment StartX=11 StartY=12 StartZ=0 EndX=0 EndY=12 EndZ=0
    g6: LineSegment StartX=0 StartY=12 StartZ=0 EndX=0 EndY=3 EndZ=0
  constraints (22):
    c: PointOnObject(g0,g-2)
    c: Horizontal(g0)
    c: Coincident(g0,g1)
    c: PointOnObject(g1,g-1)
    c: Vertical(g1)
    c: Coincident(g1,g2)
    c: PointOnObject(g2,g-1)
    c: Perpendicular(g2,g3) = 4.71239
    c: Tangent(g3,g4) = 1.5708
    c: Coincident(g4,g5)
    c: PointOnObject(g5,g-2)
    c: Horizontal(g5)
    c: Coincident(g5,g6)
    c: Coincident(g6,g0)
    c: DistanceY(g1,g1) = 3
    c: DistanceX(g2,g2) = 1
    c: DistanceY(g5) = 12
    c: Perpendicular(g4,g5)
    c: DistanceX(g5,g5) = 11
    c: DistanceX(g3,g4) = 1
    c: DistanceX(g2,g3) = 1
    c: DistanceX(g0,g0) = 8
FEATURE [PartDesign::Revolution] Revolution002
  Angle = 30
  Angle2 = 60
  Axis = (1,0,0)
  Base = (0,0,0)
  Profile = -> Sketch017
  ReferenceAxis = -> Sketch017 [H_Axis]
  Refine = true
  Suppressed = false
  Type = 0
FEATURE [Sketcher::SketchObject] Sketch018
  ArcFitTolerance = 1e-06
  AttachmentSupport = -> [XY_Plane011]
  FullyConstrained = true
  MakeInternals = false
  MapMode = 5
  expr: Constraints[10] = Sketch017.Constraints[14]
  expr: Constraints[11] = Sketch017.Constraints[16]
  sketch-geometry (7):
    g0: LineSegment StartX=0 StartY=3 StartZ=0 EndX=8 EndY=3 EndZ=0
    g1: LineSegment StartX=8 StartY=3 StartZ=0 EndX=8 EndY=0 EndZ=0
    g2: LineSegment StartX=8 StartY=0 StartZ=0 EndX=9 EndY=-2.8e-15 EndZ=0
    g3: ArcOfCircle CenterX=27.5 CenterY=-5.1e-15 CenterZ=0 NormalX=0 NormalY=0 NormalZ=1 AngleXU=0 Radius=18.5 StartAngle=2.8113 EndAngle=3.14159
    g4: LineSegment StartX=10 StartY=12 StartZ=0 EndX=0 EndY=12 EndZ=0
    g5: LineSegment StartX=0 StartY=12 StartZ=0 EndX=0 EndY=3 EndZ=0
    g6: LineSegment StartX=10 StartY=6 StartZ=0 EndX=10 EndY=12 EndZ=0
  constraints (21):
    c: Horizontal(g0)
    c: Coincident(g0,g1)
    c: PointOnObject(g1,g-1)
    c: Vertical(g1)
    c: Coincident(g1,g2)
    c: PointOnObject(g2,g-1)
    c: Perpendicular(g2,g3) = 4.71239
    c: Horizontal(g4)
    c: Coincident(g4,g5)
    c: Coincident(g5,g0)
    c: DistanceY(g1,g1) = 3
    c: DistanceY(g4) = 12
    c: DistanceX(g3) = 10
    c: Vertical(g5)
    c: PointOnObject(g0,g-2)
    c: DistanceY(g3) = 6
    c: Coincident(g6,g3)
    c: Coincident(g6,g4)
    c: Vertical(g6)
    c: DistanceX(g2,g3) = 1
    c: DistanceX(g0,g0) = 8
FEATURE [PartDesign::Revolution] Revolution003
  Angle = 30
  Angle2 = 60
  Axis = (1,0,0)
  Base = (0,0,0)
  BaseFeature = -> Revolution002
  Profile = -> Sketch018
  ReferenceAxis = -> Sketch018 [H_Axis]
  Refine = true
  Reversed = true
  Suppressed = false
  Type = 0
FEATURE [PartDesign::PolarPattern] PolarPattern001
  Angle = 360
  Axis = -> X_Axis011
  BaseFeature = -> Revolution003
  Mode = 0
  Occurrences = 6
  Offset = 120
  Refine = true
  Suppressed = false
  TransformMode = 1
FEATURE [PartDesign::Chamfer] Chamfer002
  Angle = 45
  Base = -> PolarPattern001 [Face40]
  BaseFeature = -> PolarPattern001
  ChamferType = 0
  FlipDirection = false
  Refine = true
  Size = 1
  Size2 = 1
  SupportTransform = false
  Suppressed = false
  UseAllEdges = false
FEATURE [PartDesign::Body] Body011  label="Button"
  AllowCompound = false
  Group = -> [Sketch017,Revolution002,Sketch018,Revolution003,PolarPattern001,Chamfer002]
  Origin = -> Origin011
  Placement = pos=(-3.25e-14,-71.5646,17.6465) rot=(-0.250563,-0.250563,-0.935113;1.63783rad)
  Tip = -> Chamfer002
COMPONENT P3 — recipe-attached ("Inner", modeled in this document).
Construction recipe (the document's own serialized feature program — sketch geometry with constraints, then the solid features built on it; lengths are millimeters unless a unit is written):

FEATURE [Sketcher::SketchObject] Sketch024  label="SketchInnerBottom"
  ArcFitTolerance = 1e-06
  AttachmentOffset = pos=(0,0,0) rot=(0,0,1;3.14159rad)
  AttachmentSupport = -> [XY_Plane012]
  FullyConstrained = true
  MakeInternals = false
  MapMode = 5
  Placement = pos=(0,0,0) rot=(0,0,1;3.14159rad)
  sketch-geometry (10):
    g0: LineSegment StartX=-39.5 StartY=-30 StartZ=0 EndX=39.5 EndY=-30 EndZ=0
    g1: LineSegment StartX=42.5 StartY=-27 StartZ=0 EndX=42.5 EndY=27 EndZ=0
    g2: LineSegment StartX=39.5 StartY=30 StartZ=0 EndX=-39.5 EndY=30 EndZ=0
    g3: LineSegment StartX=-42.5 StartY=27 StartZ=0 EndX=-42.5 EndY=-27 EndZ=0
    g4: ArcOfCircle CenterX=-39.5 CenterY=-27 CenterZ=0 NormalX=0 NormalY=0 NormalZ=1 AngleXU=0 Radius=3 StartAngle=3.14159 EndAngle=4.71239
    g5: ArcOfCircle CenterX=39.5 CenterY=-27 CenterZ=0 NormalX=0 NormalY=0 NormalZ=1 AngleXU=0 Radius=3 StartAngle=4.71239 EndAngle=6.28319
    g6: ArcOfCircle CenterX=39.5 CenterY=27 CenterZ=0 NormalX=0 NormalY=0 NormalZ=1 AngleXU=0 Radius=3 StartAngle=2e-16 EndAngle=1.5708
    g7: ArcOfCircle CenterX=-39.5 CenterY=27 CenterZ=0 NormalX=0 NormalY=0 NormalZ=1 AngleXU=0 Radius=3 StartAngle=1.5708 EndAngle=3.14159
    g8: GeomPoint [constr] X=42.5 Y=30 Z=0
    g9: GeomPoint [constr] X=0 Y=0 Z=0
  constraints (22):
    c: Tangent(g0,g4) = -1.5708
    c: Tangent(g0,g5) = -1.5708
    c: Tangent(g1,g5) = -1.5708
    c: Tangent(g1,g6) = -1.5708
    c: Tangent(g2,g6) = -1.5708
    c: Tangent(g2,g7) = -1.5708
    c: Tangent(g3,g7) = -1.5708
    c: Tangent(g3,g4) = -1.5708
    c: Horizontal(g0)
    c: Horizontal(g2)
    c: Vertical(g1)
    c: Vertical(g3)
    c: Equal(g4,g5)
    c: Equal(g5,g6)
    c: Equal(g6,g7)
    c: Symmetric(g2,g0,g9)
    c: PointOnObject(g8,g1)
    c: PointOnObject(g8,g2)
    c: Distance(g1,g3) = 85
    c: Distance(g0,g2) = 60
    c: Radius(g5) = 3
    c: Coincident(g9,g-1)
FEATURE [Sketcher::SketchObject] Sketch025  label="SketchInnerTop"
  ArcFitTolerance = 1e-06
  AttachmentOffset = pos=(0,0,33) rot=(0,0,1;0rad)
  AttachmentSupport = -> [XY_Plane012]
  FullyConstrained = true
  MakeInternals = false
  MapMode = 5
  Placement = pos=(0,0,33) rot=(0,0,1;0rad)
  sketch-geometry (1):
    g0: Circle CenterX=0 CenterY=0 CenterZ=0 NormalX=0 NormalY=0 NormalZ=1 AngleXU=0 Radius=50
  constraints (2):
    c: Diameter(g0) = 100
    c: Coincident(g0,g-1)
FEATURE [Sketcher::SketchObject] Sketch027
  ArcFitTolerance = 1e-06
  AttachmentSupport = -> [XY_Plane012]
  FullyConstrained = true
  MakeInternals = false
  MapMode = 5
  sketch-geometry (8):
    g0: LineSegment StartX=47.5 StartY=12 StartZ=0 EndX=67.5 EndY=12 EndZ=0
    g1: LineSegment StartX=70.5 StartY=9 StartZ=0 EndX=70.5 EndY=-11.8 EndZ=0
    g2: LineSegment StartX=67.5 StartY=-14.8 StartZ=0 EndX=47.5 EndY=-14.8 EndZ=0
    g3: LineSegment StartX=47.5 StartY=-14.8 StartZ=0 EndX=47.5 EndY=12 EndZ=0
    g4: ArcOfCircle CenterX=67.5 CenterY=9 CenterZ=0 NormalX=0 NormalY=0 NormalZ=1 AngleXU=0 Radius=3 StartAngle=0 EndAngle=1.5708
    g5: GeomPoint [constr] X=70.5 Y=12 Z=0
    g6: ArcOfCircle CenterX=67.5 CenterY=-11.8 CenterZ=0 NormalX=0 NormalY=0 NormalZ=1 AngleXU=0 Radius=3 StartAngle=4.71239 EndAngle=6.28319
    g7: GeomPoint [constr] X=70.5 Y=-14.8 Z=0
  constraints (20):
    c: DistanceX(g3) = 47.5
    c: Horizontal(g0)
    c: Vertical(g1)
    c: Horizontal(g2)
    c: Coincident(g2,g3)
    c: Vertical(g3)
    c: PointOnObject(g5,g0)
    c: PointOnObject(g5,g1)
    c: Tangent(g0,g4) = 1.5708
    c: Tangent(g1,g4) = 1.5708
    c: PointOnObject(g7,g1)
    c: PointOnObject(g7,g2)
    c: Tangent(g1,g6) = 1.5708
    c: Tangent(g2,g6) = 1.5708
    c: Equal(g6,g4)
    c: Radius(g4) = 3
    c: Coincident(g3,g0)
    c: DistanceX(g0,g0) = 20
    c: DistanceY(g0) = 12
    c: DistanceY(g2) = -14.8
FEATURE [PartDesign::FeatureBase] BaseFeature
  BaseFeature = -> Cut002
  Suppressed = false
FEATURE [Sketcher::SketchObject] Sketch028
  ArcFitTolerance = 1e-06
  AttachmentOffset = pos=(0,0,10) rot=(0,0,1;0rad)
  AttachmentSupport = -> [XY_Plane012]
  FullyConstrained = true
  MakeInternals = false
  MapMode = 5
  Placement = pos=(0,0,10) rot=(0,0,1;0rad)
  sketch-geometry (11):
    g0: LineSegment StartX=40 StartY=6.8 StartZ=0 EndX=40 EndY=-9.1 EndZ=0
    g1: LineSegment StartX=40 StartY=6.8 StartZ=0 EndX=64.5 EndY=6.8 EndZ=0
    g2: LineSegment StartX=40 StartY=-9.1 StartZ=0 EndX=71.5 EndY=-9.1 EndZ=0
    g3: ArcOfCircle CenterX=64.5 CenterY=5.8 CenterZ=0 NormalX=0 NormalY=0 NormalZ=1 AngleXU=0 Radius=1 StartAngle=0 EndAngle=1.5708
    g4: GeomPoint [constr] X=65.5 Y=6.8 Z=0
    g5: GeomPoint [constr] X=65.5 Y=-9.1 Z=0
    g6: LineSegment StartX=65.5 StartY=5.8 StartZ=0 EndX=65.5 EndY=-7.1 EndZ=0
    g7: LineSegment StartX=66.5 StartY=-8.1 StartZ=0 EndX=71.5 EndY=-8.1 EndZ=0
    g8: LineSegment StartX=71.5 StartY=-8.1 StartZ=0 EndX=71.5 EndY=-9.1 EndZ=0
    g9: ArcOfCircle CenterX=66.5 CenterY=-7.1 CenterZ=0 NormalX=0 NormalY=0 NormalZ=1 AngleXU=0 Radius=1 StartAngle=3.14159 EndAngle=4.71239
    g10: GeomPoint [constr] X=65.5 Y=-8.1 Z=0
  constraints (28):
    c: Vertical(g0)
    c: DistanceX(g0) = 40
    c: Horizontal(g1)
    c: Horizontal(g2)
    c: DistanceY(g5,g-1) = 9.1
    c: DistanceY(g4) = 6.8
    c: Coincident(g1,g0)
    c: Coincident(g2,g0)
    c: DistanceX(g1,g4) = 25.5
    c: PointOnObject(g4,g1)
    c: Tangent(g1,g3) = 1.5708
    c: PointOnObject(g5,g2)
    c: Radius(g3) = 1
    c: Vertical(g6)
    c: PointOnObject(g4,g6)
    c: PointOnObject(g5,g6)
    c: Horizontal(g7)
    c: Coincident(g7,g8)
    c: Coincident(g8,g2)
    c: Vertical(g8)
    c: DistanceY(g8,g8) = 1
    c: PointOnObject(g10,g6)
    c: PointOnObject(g10,g7)
    c: Tangent(g6,g9) = -1.5708
    c: Tangent(g7,g9) = -1.5708
    c: Equal(g9,g3)
    c: DistanceX(g7,g7) = 5
    c: Tangent(g6,g3) = 1.5708
FEATURE [Sketcher::SketchObject] Sketch029
  ArcFitTolerance = 1e-06
  AttachmentOffset = pos=(0,0,26) rot=(0,0,1;0rad)
  AttachmentSupport = -> [XY_Plane012]
  FullyConstrained = true
  MakeInternals = false
  MapMode = 5
  Placement = pos=(0,0,26) rot=(0,0,1;0rad)
  sketch-geometry (8):
    g0: LineSegment StartX=49.5 StartY=12.3 StartZ=0 EndX=67.5 EndY=12.3 EndZ=0
    g1: LineSegment StartX=70.5 StartY=9.3 StartZ=0 EndX=70.5 EndY=-11.8 EndZ=0
    g2: LineSegment StartX=67.5 StartY=-14.8 StartZ=0 EndX=49.5 EndY=-14.8 EndZ=0
    g3: LineSegment StartX=49.5 StartY=-14.8 StartZ=0 EndX=49.5 EndY=12.3 EndZ=0
    g4: ArcOfCircle CenterX=67.5 CenterY=9.3 CenterZ=0 NormalX=0 NormalY=0 NormalZ=1 AngleXU=0 Radius=3 StartAngle=2e-16 EndAngle=1.5708
    g5: GeomPoint [constr] X=70.5 Y=12.3 Z=0
    g6: ArcOfCircle CenterX=67.5 CenterY=-11.8 CenterZ=0 NormalX=0 NormalY=0 NormalZ=1 AngleXU=0 Radius=3 StartAngle=4.71239 EndAngle=6.28319
    g7: GeomPoint [constr] X=70.5 Y=-14.8 Z=0
  constraints (20):
    c: DistanceX(g3) = 49.5
    c: Horizontal(g0)
    c: Vertical(g1)
    c: Horizontal(g2)
    c: Coincident(g2,g3)
    c: Vertical(g3)
    c: PointOnObject(g5,g0)
    c: PointOnObject(g5,g1)
    c: Tangent(g0,g4) = 1.5708
    c: Tangent(g1,g4) = 1.5708
    c: PointOnObject(g7,g1)
    c: PointOnObject(g7,g2)
    c: Tangent(g1,g6) = 1.5708
    c: Tangent(g2,g6) = 1.5708
    c: Equal(g6,g4)
    c: Radius(g4) = 3
    c: Coincident(g3,g0)
    c: DistanceY(g0) = 12.3
    c: DistanceY(g2) = -14.8
    c: DistanceX(g0,g0) = 18
FEATURE [PartDesign::AdditiveLoft] AdditiveLoft  label="AdditiveLC"
  BaseFeature = -> BaseFeature
  Closed = false
  Profile = -> Sketch027
  Refine = true
  Ruled = false
  Sections = -> [Sketch029]
  Suppressed = false
FEATURE [PartDesign::Pocket] Pocket003  label="PocketLC"
  BaseFeature = -> AdditiveLoft
  Direction = (0,0,-1)
  Length = 14
  Length2 = 5
  Profile = -> Sketch028
  ReferenceAxis = -> Sketch028 [N_Axis]
  Refine = true
  Reversed = true
  Suppressed = false
  Type = 0
FEATURE [Sketcher::SketchObject] Sketch030
  ArcFitTolerance = 1e-06
  AttachmentOffset = pos=(0,0,0) rot=(0,0,1;-1.5708rad)
  AttachmentSupport = -> [XY_Plane012]
  FullyConstrained = false
  MakeInternals = false
  MapMode = 5
  Placement = pos=(0,0,0) rot=(0,0,1;4.71239rad)
  sketch-geometry (65):
    g0: LineSegment StartX=-35 StartY=6 StartZ=0 EndX=-35 EndY=-6 EndZ=0
    g1: LineSegment StartX=-35 StartY=-6 StartZ=0 EndX=35 EndY=-6 EndZ=0
    g2: LineSegment StartX=35 StartY=-6 StartZ=0 EndX=35 EndY=6 EndZ=0
    g3: LineSegment StartX=35 StartY=6 StartZ=0 EndX=-35 EndY=6 EndZ=0
    g4: Circle CenterX=0 CenterY=0 CenterZ=0 NormalX=0 NormalY=0 NormalZ=1 AngleXU=0 Radius=2.8
    g5: LineSegment StartX=-58 StartY=11 StartZ=0 EndX=-88 EndY=11 EndZ=0
    g6: LineSegment StartX=-88 StartY=11 StartZ=0 EndX=-88 EndY=-11 EndZ=0
    g7: LineSegment StartX=-88 StartY=-11 StartZ=0 EndX=-58 EndY=-11 EndZ=0
    g8: LineSegment StartX=-58 StartY=-11 StartZ=0 EndX=-58 EndY=-9 EndZ=0
    g9: LineSegment StartX=-85.5 StartY=8 StartZ=0 EndX=-85.5 EndY=-8 EndZ=0
    g10: LineSegment StartX=-84.5 StartY=-9 StartZ=0 EndX=-77.5 EndY=-9 EndZ=0
    g11: LineSegment StartX=-58 StartY=9 StartZ=0 EndX=-59.5 EndY=9 EndZ=0
    g12: LineSegment StartX=-58 StartY=11 StartZ=0 EndX=-58 EndY=9 EndZ=0
    g13: LineSegment StartX=-63.5 StartY=-8 StartZ=0 EndX=-63.5 EndY=-3.5 EndZ=0
    g14: LineSegment StartX=-64.5 StartY=-2.5 StartZ=0 EndX=-68.9 EndY=-2.5 EndZ=0
    g15: LineSegment StartX=-69.9 StartY=-1.5 StartZ=0 EndX=-69.9 EndY=1.5 EndZ=0
    g16: LineSegment StartX=-68.9 StartY=2.5 StartZ=0 EndX=-64.5 EndY=2.5 EndZ=0
    g17: LineSegment StartX=-63.5 StartY=3.5 StartZ=0 EndX=-63.5 EndY=8 EndZ=0
    g18: LineSegment StartX=-60.5 StartY=8 StartZ=0 EndX=-60.5 EndY=-8 EndZ=0
    g19: LineSegment StartX=-64.5 StartY=9 StartZ=0 EndX=-71.5 EndY=9 EndZ=0
    g20: LineSegment StartX=-59.5 StartY=-9 StartZ=0 EndX=-58 EndY=-9 EndZ=0
    g21: ArcOfCircle CenterX=-59.5 CenterY=8 CenterZ=0 NormalX=0 NormalY=0 NormalZ=1 AngleXU=0 Radius=1 StartAngle=1.5708 EndAngle=3.14159
    g22: GeomPoint [constr] X=-60.5 Y=9 Z=0
    g23: ArcOfCircle CenterX=-59.5 CenterY=-8 CenterZ=0 NormalX=0 NormalY=0 NormalZ=1 AngleXU=0 Radius=1 StartAngle=3.14159 EndAngle=4.71239
    g24: GeomPoint [constr] X=-60.5 Y=-9 Z=0
    g25: ArcOfCircle CenterX=-64.5 CenterY=-8 CenterZ=0 NormalX=0 NormalY=0 NormalZ=1 AngleXU=0 Radius=1 StartAngle=4.71239 EndAngle=6.28319
    g26: GeomPoint [constr] X=-63.5 Y=-9 Z=0
    g27: ArcOfCircle CenterX=-64.5 CenterY=-3.5 CenterZ=0 NormalX=0 NormalY=0 NormalZ=1 AngleXU=0 Radius=1 StartAngle=0 EndAngle=1.5708
    g28: GeomPoint [constr] X=-63.5 Y=-2.5 Z=0
    g29: ArcOfCircle CenterX=-64.5 CenterY=3.5 CenterZ=0 NormalX=0 NormalY=0 NormalZ=1 AngleXU=0 Radius=1 StartAngle=4.71239 EndAngle=6.28319
    g30: GeomPoint [constr] X=-63.5 Y=2.5 Z=0
    g31: ArcOfCircle CenterX=-84.5 CenterY=8 CenterZ=0 NormalX=0 NormalY=0 NormalZ=1 AngleXU=0 Radius=1 StartAngle=1.5708 EndAngle=3.14159
    g32: GeomPoint [constr] X=-85.5 Y=9 Z=0
    g33: ArcOfCircle CenterX=-84.5 CenterY=-8 CenterZ=0 NormalX=0 NormalY=0 NormalZ=1 AngleXU=0 Radius=1 StartAngle=3.14159 EndAngle=4.71239
    g34: GeomPoint [constr] X=-85.5 Y=-9 Z=0
    g35: LineSegment StartX=-76.5 StartY=8 StartZ=0 EndX=-76.5 EndY=6.6 EndZ=0
    g36: LineSegment StartX=-75.5 StartY=5.6 StartZ=0 EndX=-73.5 EndY=5.6 EndZ=0
    g37: LineSegment StartX=-72.5 StartY=6.6 StartZ=0 EndX=-72.5 EndY=8 EndZ=0
    g38: LineSegment StartX=-76.5 StartY=-8 StartZ=0 EndX=-76.5 EndY=-6.6 EndZ=0
    g39: LineSegment StartX=-75.5 StartY=-5.6 StartZ=0 EndX=-73.5 EndY=-5.6 EndZ=0
    g40: LineSegment StartX=-72.5 StartY=-6.6 StartZ=0 EndX=-72.5 EndY=-8 EndZ=0
    g41: LineSegment StartX=-71.5 StartY=-9 StartZ=0 EndX=-64.5 EndY=-9 EndZ=0
    g42: LineSegment StartX=-77.5 StartY=9 StartZ=0 EndX=-84.5 EndY=9 EndZ=0
    g43: ArcOfCircle CenterX=-71.5 CenterY=8 CenterZ=0 NormalX=0 NormalY=0 NormalZ=1 AngleXU=0 Radius=1 StartAngle=1.5708 EndAngle=3.14159
    g44: GeomPoint [constr] X=-72.5 Y=9 Z=0
    g45: ArcOfCircle CenterX=-73.5 CenterY=6.6 CenterZ=0 NormalX=0 NormalY=0 NormalZ=1 AngleXU=0 Radius=1 StartAngle=4.71239 EndAngle=6.28319
    g46: GeomPoint [constr] X=-72.5 Y=5.6 Z=0
    g47: ArcOfCircle CenterX=-75.5 CenterY=6.6 CenterZ=0 NormalX=0 NormalY=0 NormalZ=1 AngleXU=0 Radius=1 StartAngle=3.14159 EndAngle=4.71239
    g48: GeomPoint [constr] X=-76.5 Y=5.6 Z=0
    g49: ArcOfCircle CenterX=-77.5 CenterY=8 CenterZ=0 NormalX=0 NormalY=0 NormalZ=1 AngleXU=0 Radius=1 StartAngle=0 EndAngle=1.5708
    g50: GeomPoint [constr] X=-76.5 Y=9 Z=0
    g51: ArcOfCircle CenterX=-71.5 CenterY=-8 CenterZ=0 NormalX=0 NormalY=0 NormalZ=1 AngleXU=0 Radius=1 StartAngle=3.14159 EndAngle=4.71239
    g52: GeomPoint [constr] X=-72.5 Y=-9 Z=0
    g53: ArcOfCircle CenterX=-73.5 CenterY=-6.6 CenterZ=0 NormalX=0 NormalY=0 NormalZ=1 AngleXU=0 Radius=1 StartAngle=0 EndAngle=1.5708
    g54: GeomPoint [constr] X=-72.5 Y=-5.6 Z=0
    g55: ArcOfCircle CenterX=-75.5 CenterY=-6.6 CenterZ=0 NormalX=0 NormalY=0 NormalZ=1 AngleXU=0 Radius=1 StartAngle=1.5708 EndAngle=3.14159
    g56: GeomPoint [constr] X=-76.5 Y=-5.6 Z=0
    g57: ArcOfCircle CenterX=-77.5 CenterY=-8 CenterZ=0 NormalX=0 NormalY=0 NormalZ=1 AngleXU=0 Radius=1 StartAngle=4.71239 EndAngle=6.28319
    g58: GeomPoint [constr] X=-76.5 Y=-9 Z=0
    g59: ArcOfCircle CenterX=-64.5 CenterY=8 CenterZ=0 NormalX=0 NormalY=0 NormalZ=1 AngleXU=0 Radius=1 StartAngle=0 EndAngle=1.5708
    g60: GeomPoint [constr] X=-63.5 Y=9 Z=0
    g61: ArcOfCircle CenterX=-68.9 CenterY=1.5 CenterZ=0 NormalX=0 NormalY=0 NormalZ=1 AngleXU=0 Radius=1 StartAngle=1.5708 EndAngle=3.14159
    g62: GeomPoint [constr] X=-69.9 Y=2.5 Z=0
    g63: ArcOfCircle CenterX=-68.9 CenterY=-1.5 CenterZ=0 NormalX=0 NormalY=0 NormalZ=1 AngleXU=0 Radius=1 StartAngle=3.14159 EndAngle=4.71239
    g64: GeomPoint [constr] X=-69.9 Y=-2.5 Z=0
  constraints (154):
    c: Coincident(g0,g1)
    c: Coincident(g1,g2)
    c: Coincident(g2,g3)
    c: Coincident(g3,g0)
    c: Vertical(g0)
    c: Vertical(g2)
    c: Horizontal(g1)
    c: Horizontal(g3)
    c: Distance(g0,g2) = 70
    c: Symmetric(g0,g2,g-1)
    c: DistanceY(g0,g0) = 12
    c: Diameter(g4) = 5.6
    c: Coincident(g4,g-1)
    c: Coincident(g5,g6)
    c: Coincident(g6,g7)
    c: Coincident(g7,g8)
    c: Horizontal(g5)
    c: Horizontal(g7)
    c: Vertical(g8)
    c: Symmetric(g6,g5,g-1)
    c: DistanceX(g5) = -58
    c: DistanceX(g5,g5) = 30
    c: Vertical(g9)
    c: Horizontal(g10)
    c: Horizontal(g11)
    c: Coincident(g8,g20)
    c: Coincident(g12,g5)
    c: Coincident(g12,g11)
    c: Vertical(g12)
    c: DistanceX(g34) = -85.5
    c: Vertical(g13)
    c: Horizontal(g14)
    c: Horizontal(g16)
    c: Vertical(g17)
    c: Vertical(g18)
    c: PointOnObject(g22,g11)
    c: PointOnObject(g22,g18)
    c: Tangent(g11,g21) = -1.5708
    c: Tangent(g18,g21) = -1.5708
    c: Horizontal(g20)
    c: Horizontal(g26,g24)
    c: PointOnObject(g24,g18)
    c: PointOnObject(g24,g20)
    c: Tangent(g18,g23) = -1.5708
    c: Tangent(g20,g23) = -1.5708
    c: PointOnObject(g26,g41)
    c: PointOnObject(g26,g13)
    c: Coincident(g41,g25) = -1.5708
    c: Tangent(g13,g25) = -1.5708
    c: PointOnObject(g28,g13)
    c: PointOnObject(g28,g14)
    c: Tangent(g13,g27) = -1.5708
    c: Tangent(g14,g27) = -1.5708
    c: PointOnObject(g30,g16)
    c: PointOnObject(g30,g17)
    c: Tangent(g16,g29) = -1.5708
    c: Tangent(g17,g29) = -1.5708
    c: PointOnObject(g32,g9)
    c: PointOnObject(g32,g42)
    c: Tangent(g9,g31) = -1.5708
    c: PointOnObject(g34,g9)
    c: PointOnObject(g34,g10)
    c: Tangent(g9,g33) = -1.5708
    c: Tangent(g10,g33) = -1.5708
    c: Vertical(g35)
    c: Horizontal(g36)
    c: Vertical(g37)
    c: Vertical(g38)
    c: Horizontal(g39)
    c: Vertical(g40)
    c: PointOnObject(g44,g19)
    c: PointOnObject(g44,g37)
    c: Tangent(g19,g43) = -1.5708
    c: Tangent(g37,g43) = 1.5708
    c: PointOnObject(g46,g36)
    c: PointOnObject(g46,g37)
    c: Tangent(g36,g45) = -1.5708
    c: Tangent(g37,g45) = -1.5708
    c: PointOnObject(g48,g35)
    c: PointOnObject(g48,g36)
    c: Tangent(g35,g47) = -1.5708
    c: Tangent(g36,g47) = -1.5708
    c: PointOnObject(g50,g35)
    c: PointOnObject(g50,g42)
    c: Tangent(g35,g49) = 1.5708
    c: Tangent(g42,g49) = -1.5708
    c: PointOnObject(g52,g40)
    c: PointOnObject(g52,g41)
    c: Tangent(g40,g51) = -1.5708
    c: Tangent(g41,g51) = -1.5708
    c: PointOnObject(g54,g39)
    c: PointOnObject(g54,g40)
    c: Tangent(g39,g53) = 1.5708
    c: Tangent(g40,g53) = 1.5708
    c: PointOnObject(g56,g38)
    c: PointOnObject(g56,g39)
    c: Tangent(g38,g55) = 1.5708
    c: Tangent(g39,g55) = 1.5708
    c: PointOnObject(g58,g10)
    c: PointOnObject(g58,g38)
    c: Tangent(g10,g57) = -1.5708
    c: Tangent(g38,g57) = -1.5708
    c: Equal(g57,g55)
    c: Equal(g55,g53)
    c: Equal(g53,g51)
    c: Equal(g51,g25)
    c: Equal(g25,g27)
    c: Equal(g27,g29)
    c: Equal(g29,g43)
    c: Equal(g43,g45)
    c: Equal(g45,g47)
    c: Equal(g47,g49)
    c: Equal(g49,g23)
    c: Equal(g23,g21)
    c: Horizontal(g22,g60)
    c: Horizontal(g19)
    c: Horizontal(g42)
    c: Horizontal(g41)
    c: Horizontal(g58,g52)
    c: PointOnObject(g60,g17)
    c: PointOnObject(g60,g19)
    c: Tangent(g17,g59) = -1.5708
    c: Tangent(g19,g59) = -1.5708
    c: Equal(g59,g21)
    c: PointOnObject(g62,g15)
    c: PointOnObject(g62,g16)
    c: Tangent(g15,g61) = 1.5708
    c: Tangent(g16,g61) = 1.5708
    c: PointOnObject(g64,g14)
    c: PointOnObject(g64,g15)
    c: Tangent(g14,g63) = 1.5708
    c: Tangent(g15,g63) = 1.5708
    c: Equal(g63,g61)
    c: Equal(g61,g45)
    c: Horizontal(g44,g50)
    c: Symmetric(g63,g61,g-1)
    c: DistanceX(g17,g18) = 3
    c: DistanceX(g35,g37) = 4
    c: Equal(g42,g19)
    c: Vertical(g55,g47)
    c: Equal(g19,g41)
    c: Equal(g13,g17)
    c: DistanceY(g36) = 5.6
    c: Symmetric(g39,g36,g-1)
    c: DistanceY(g8) = -9
    c: Radius(g31) = 1
    c: Tangent(g42,g31) = -1.5708
    c: Equal(g31,g49)
    c: Equal(g33,g31)
    c: DistanceY(g8,g8) = 2
    c: DistanceX(g9,g17) = 22
    c: Vertical(g8,g11)
    c: DistanceX(g9,g15) = 15.6
    c: DistanceY(g14,g16) = 5
FEATURE [PartDesign::Pad] Pad019  label="PadUSBAkkuSteg"
  BaseFeature = -> Pocket003
  Direction = (0,0,1)
  Length = 8
  Length2 = 10
  Profile = -> Sketch030
  ReferenceAxis = -> Sketch030 [N_Axis]
  Refine = true
  Suppressed = false
  Type = 0
FEATURE [Sketcher::SketchObject] Sketch031
  ArcFitTolerance = 1e-06
  AttachmentSupport = -> [YZ_Plane012]
  FullyConstrained = true
  MakeInternals = false
  MapMode = 5
  Placement = pos=(0,0,0) rot=(0.57735,0.57735,0.57735;2.0944rad)
  sketch-geometry (14):
    g0: LineSegment StartX=57.25 StartY=0 StartZ=0 EndX=57.25 EndY=5.5 EndZ=0
    g1: LineSegment StartX=38.75 StartY=0 StartZ=0 EndX=38.75 EndY=5.5 EndZ=0
    g2: LineSegment StartX=57.25 StartY=0 StartZ=0 EndX=59.25 EndY=0 EndZ=0
    g3: LineSegment StartX=59.25 StartY=0 StartZ=0 EndX=59.25 EndY=5.5 EndZ=0
    g4: LineSegment StartX=36.75 StartY=5.5 StartZ=0 EndX=34.75 EndY=0 EndZ=0
    g5: LineSegment StartX=34.75 StartY=0 StartZ=0 EndX=38.75 EndY=0 EndZ=0
    g6: ArcOfCircle CenterX=48 CenterY=5.5 CenterZ=0 NormalX=0 NormalY=0 NormalZ=1 AngleXU=0 Radius=9.25 StartAngle=2.35619 EndAngle=3.14159
    g7: ArcOfCircle CenterX=48 CenterY=5.5 CenterZ=0 NormalX=0 NormalY=0 NormalZ=1 AngleXU=0 Radius=9.25 StartAngle=0 EndAngle=0.785398
    g8: ArcOfCircle CenterX=48 CenterY=5.5 CenterZ=0 NormalX=0 NormalY=0 NormalZ=1 AngleXU=0 Radius=11.25 StartAngle=0 EndAngle=0.785398
    g9: ArcOfCircle CenterX=48 CenterY=5.5 CenterZ=0 NormalX=0 NormalY=0 NormalZ=1 AngleXU=0 Radius=11.25 StartAngle=2.35619 EndAngle=3.14159
    g10: LineSegment StartX=40.045 StartY=13.455 StartZ=0 EndX=41.4593 EndY=12.0407 EndZ=0
    g11: LineSegment StartX=54.5407 StartY=12.0407 StartZ=0 EndX=45.3483 EndY=21.2331 EndZ=0
    g12: LineSegment StartX=45.3483 StartY=21.2331 StartZ=0 EndX=46.7626 EndY=22.6473 EndZ=0
    g13: LineSegment StartX=46.7626 StartY=22.6473 StartZ=0 EndX=55.955 EndY=13.455 EndZ=0
  constraints (39):
    c: PointOnObject(g0,g-1)
    c: Tangent(g0,g7) = -1.5708
    c: Horizontal(g1,g0)
    c: Vertical(g0)
    c: DistanceX(g1,g0) = 18.5
    c: Coincident(g1,g6)
    c: Vertical(g1)
    c: DistanceY(g7) = 5.5
    c: DistanceX(g7) = 48
    c: Coincident(g0,g2)
    c: PointOnObject(g2,g-1)
    c: Coincident(g2,g3)
    c: Vertical(g3)
    c: Tangent(g3,g8) = -1.5708
    c: Coincident(g9,g4)
    c: PointOnObject(g4,g-1)
    c: Coincident(g4,g5)
    c: Coincident(g5,g1)
    c: DistanceX(g2,g2) = 2
    c: Coincident(g8,g7)
    c: Horizontal(g6,g3)
    c: DistanceX(g9,g6) = 2
    c: Coincident(g7,g6)
    c: Equal(g8,g9)
    c: Equal(g6,g7)
    c: Coincident(g6,g9)
    c: Coincident(g10,g9)
    c: Coincident(g10,g6)
    c: Perpendicular(g6,g10)
    c: Horizontal(g6,g7)
    c: Tangent(g7,g11) = -1.5708
    c: Coincident(g11,g12)
    c: Coincident(g12,g13)
    c: Angle(g11,g-1) = 0.785398
    c: Parallel(g13,g11)
    c: Tangent(g13,g8) = 1.5708
    c: DistanceX(g5,g5) = 4
    c: Distance(g11,g11) = 13
    c: Perpendicular(g13,g12)
FEATURE [PartDesign::Pad] Pad020  label="PadYZAkku"
  BaseFeature = -> Pad019
  Direction = (1,0,0)
  Length = 33
  Length2 = 10
  Midplane = true
  Profile = -> Sketch031
  ReferenceAxis = -> Sketch031 [N_Axis]
  Refine = true
  Suppressed = false
  Type = 0
FEATURE [Sketcher::SketchObject] Sketch032
  ArcFitTolerance = 1e-06
  AttachmentSupport = -> [XZ_Plane012]
  FullyConstrained = false
  MakeInternals = false
  MapMode = 5
  Placement = pos=(0,0,0) rot=(1,0,0;1.5708rad)
  sketch-geometry (16):
    g0: LineSegment StartX=-79.4871 StartY=15.1925 StartZ=0 EndX=-62.5 EndY=25 EndZ=0
    g1: LineSegment StartX=-79.4871 StartY=15.1925 StartZ=0 EndX=-77.7551 EndY=18.1925 EndZ=0
    g2: LineSegment StartX=-77.7551 StartY=18.1925 StartZ=0 EndX=-62.5 EndY=27 EndZ=0
    g3: LineSegment StartX=-62.5 StartY=27 StartZ=0 EndX=-62.5 EndY=25 EndZ=0
    g4: LineSegment StartX=-58.3 StartY=42.4629 StartZ=0 EndX=-55.5831 EndY=42.4629 EndZ=0
    g5: LineSegment StartX=-55.5831 StartY=42.4629 StartZ=0 EndX=-50.933 EndY=24.6909 EndZ=0
    g6: LineSegment StartX=-50.933 StartY=24.6909 StartZ=0 EndX=-58.3 EndY=24.6909 EndZ=0
    g7: LineSegment StartX=-58.3 StartY=24.6909 StartZ=0 EndX=-58.3 EndY=42.4629 EndZ=0
    g8: LineSegment StartX=-76.023 StartY=21.1925 StartZ=0 EndX=-74.291 EndY=24.1925 EndZ=0
    g9: LineSegment StartX=-74.291 StartY=24.1925 StartZ=0 EndX=-62.5 EndY=31 EndZ=0
    g10: LineSegment StartX=-62.5 StartY=31 StartZ=0 EndX=-62.5 EndY=29 EndZ=0
    g11: LineSegment StartX=-62.5 StartY=29 StartZ=0 EndX=-76.023 EndY=21.1925 EndZ=0
    g12: LineSegment StartX=-72.5589 StartY=27.1925 StartZ=0 EndX=-70.8269 EndY=30.1925 EndZ=0
    g13: LineSegment StartX=-70.8269 StartY=30.1925 StartZ=0 EndX=-62.5 EndY=35 EndZ=0
    g14: LineSegment StartX=-62.5 StartY=35 StartZ=0 EndX=-62.5 EndY=33 EndZ=0
    g15: LineSegment StartX=-62.5 StartY=33 StartZ=0 EndX=-72.5589 EndY=27.1925 EndZ=0
  constraints (41):
    c: DistanceY(g0) = 25
    c: Angle(g-1,g0) = 0.523599
    c: Coincident(g1,g0)
    c: Coincident(g1,g2)
    c: Parallel(g2,g0)
    c: Coincident(g3,g2)
    c: Coincident(g3,g0)
    c: Vertical(g3)
    c: DistanceY(g3,g3) = 2
    c: DistanceX(g2) = -62.5
    c: Coincident(g4,g5)
    c: Coincident(g5,g6)
    c: Coincident(g6,g7)
    c: Coincident(g7,g4)
    c: Vertical(g7)
    c: Horizontal(g6)
    c: Horizontal(g4)
    c: DistanceX(g4) = -58.3
    c: Coincident(g8,g9)
    c: Coincident(g9,g10)
    c: Vertical(g10)
    c: Coincident(g10,g11)
    c: Coincident(g11,g8)
    c: Parallel(g11,g9)
    c: Parallel(g11,g2)
    c: DistanceY(g10,g10) = 2
    c: Coincident(g12,g13)
    c: Coincident(g13,g14)
    c: Vertical(g14)
    c: Coincident(g14,g15)
    c: Coincident(g15,g12)
    c: Parallel(g13,g15)
    c: Parallel(g15,g9)
    c: DistanceY(g14,g14) = 2
    c: DistanceY(g9,g14) = 2
    c: DistanceY(g2,g10) = 2
    c: Tangent(g1,g8)
    c: Tangent(g12,g8)
    c: Angle(g0,g1) = 0.523599
    c: Vertical(g14,g9)
    c: Vertical(g10,g2)
FEATURE [PartDesign::Pad] Pad021  label="PadESPMount"
  BaseFeature = -> Pad020
  Direction = (0,-1,2e-16)
  Length = 9
  Length2 = 10
  Midplane = true
  Profile = -> Sketch032
  ReferenceAxis = -> Sketch032 [N_Axis]
  Refine = true
  Suppressed = false
  Type = 0
FEATURE [PartDesign::SubShapeBinder] Binder016  label="BinderEncoder"
  BindCopyOnChange = 0
  BindMode = 0
  ClaimChildren = false
  Context = -> Body012 [Binder016.]
  Fuse = false
  MakeFace = true
  OffsetFill = false
  OffsetIntersection = false
  OffsetJoinType = 0
  OffsetOpenResult = false
  PartialLoad = false
  Refine = true
  Relative = true
  Support = -> [Link006[Pad012.Face18]]
  _Version = 2
FEATURE [Sketcher::SketchObject] Sketch033
  ArcFitTolerance = 1e-06
  AttachmentSupport = -> [YZ_Plane012]
  FullyConstrained = true
  MakeInternals = false
  MapMode = 5
  Placement = pos=(0,0,0) rot=(0.57735,0.57735,0.57735;2.0944rad)
  sketch-geometry (4):
    g0: LineSegment StartX=-73.5 StartY=0 StartZ=0 EndX=-52.2 EndY=36.8927 EndZ=0
    g1: LineSegment StartX=-88.3 StartY=0 StartZ=0 EndX=-73.5 EndY=0 EndZ=0
    g2: LineSegment StartX=-88.3 StartY=0 StartZ=0 EndX=-63.3 EndY=43.3013 EndZ=0
    g3: LineSegment StartX=-63.3 StartY=43.3013 StartZ=0 EndX=-52.2 EndY=36.8927 EndZ=0
  constraints (12):
    c: PointOnObject(g1,g-1)
    c: Coincident(g1,g0)
    c: Horizontal(g1)
    c: Coincident(g2,g1)
    c: Angle(g1,g2) = 1.0472
    c: Coincident(g3,g0)
    c: Perpendicular(g0,g3)
    c: DistanceX(g0) = -73.5
    c: DistanceX(g1,g1) = 14.8
    c: Coincident(g2,g3)
    c: Distance(g2,g2) = 50
    c: Parallel(g0,g2)
FEATURE [PartDesign::Pad] Pad022  label="PadEncoderBlock"
  BaseFeature = -> Pad021
  Direction = (1,0,0)
  Length = 28
  Length2 = 10
  Midplane = true
  Profile = -> Sketch033
  ReferenceAxis = -> Sketch033 [N_Axis]
  Refine = true
  Suppressed = false
  Type = 0
FEATURE [PartDesign::SubShapeBinder] Binder017  label="BinderDisplay"
  BindCopyOnChange = 0
  BindMode = 0
  ClaimChildren = false
  Context = -> Body012 [Binder017.]
  Fuse = false
  MakeFace = true
  OffsetFill = false
  OffsetIntersection = false
  OffsetJoinType = 0
  OffsetOpenResult = false
  PartialLoad = false
  Refine = true
  Relative = true
  _Version = 2
FEATURE [PartDesign::SubShapeBinder] Binder018
  BindCopyOnChange = 0
  BindMode = 0
  ClaimChildren = false
  Context = -> Body012 [Binder018.]
  Fuse = false
  MakeFace = true
  OffsetFill = false
  OffsetIntersection = false
  OffsetJoinType = 0
  OffsetOpenResult = false
  PartialLoad = false
  Refine = true
  Relative = true
  Support = -> [CompoundFilter[Face16]]
  _Version = 2
FEATURE [Sketcher::SketchObject] Sketch042
  ArcFitTolerance = 1e-06
  AttachmentSupport = -> [YZ_Plane012]
  FullyConstrained = true
  MakeInternals = false
  MapMode = 5
  Placement = pos=(0,0,0) rot=(0.57735,0.57735,0.57735;2.0944rad)
  sketch-geometry (4):
    g0: LineSegment StartX=-34.05 StartY=-0.05 StartZ=0 EndX=-33.5 EndY=0.902628 EndZ=0
    g1: LineSegment StartX=-33.5 StartY=0.902628 StartZ=0 EndX=-32.5 EndY=0.902628 EndZ=0
    g2: LineSegment StartX=-32.5 StartY=0.902628 StartZ=0 EndX=-31.95 EndY=-0.05 EndZ=0
    g3: LineSegment StartX=-31.95 StartY=-0.05 StartZ=0 EndX=-34.05 EndY=-0.05 EndZ=0
  constraints (12):
    c: Coincident(g0,g1)
    c: Horizontal(g1)
    c: Coincident(g1,g2)
    c: Coincident(g2,g3)
    c: Coincident(g3,g0)
    c: Horizontal(g3)
    c: Angle(g3,g0) = 1.0472
    c: Equal(g0,g2)
    c: DistanceX(g3,g3) = 2.1
    c: DistanceX(g1,g1) = 1
    c: DistanceX(g2) = -31.95
    c: DistanceY(g2) = -0.05
FEATURE [Sketcher::SketchObject] Sketch051
  ArcFitTolerance = 1e-06
  AttachmentSupport = -> [XY_Plane012]
  FullyConstrained = true
  MakeInternals = false
  MapMode = 5
  sketch-geometry (12):
    g0: LineSegment StartX=-36.5 StartY=45 StartZ=0 EndX=-42.5 EndY=45 EndZ=0
    g1: LineSegment StartX=-48.5 StartY=39 StartZ=0 EndX=-48.5 EndY=28 EndZ=0
    g2: LineSegment StartX=-48.5 StartY=28 StartZ=0 EndX=-42.5 EndY=28 EndZ=0
    g3: LineSegment StartX=-33.5 StartY=39 StartZ=0 EndX=-33.5 EndY=42 EndZ=0
    g4: ArcOfCircle CenterX=-42.5 CenterY=39 CenterZ=0 NormalX=0 NormalY=0 NormalZ=1 AngleXU=0 Radius=6 StartAngle=1.5708 EndAngle=3.14159
    g5: GeomPoint [constr] X=-48.5 Y=45 Z=0
    g6: LineSegment StartX=-30.5 StartY=33 StartZ=0 EndX=-42.5 EndY=33 EndZ=0
    g7: LineSegment StartX=-42.5 StartY=33 StartZ=0 EndX=-42.5 EndY=28 EndZ=0
    g8: ArcOfCircle CenterX=-30.5 CenterY=39 CenterZ=0 NormalX=0 NormalY=0 NormalZ=1 AngleXU=0 Radius=3 StartAngle=3.14159 EndAngle=4.71239
    g9: LineSegment StartX=-30.5 StartY=36 StartZ=0 EndX=-30.5 EndY=33 EndZ=0
    g10: ArcOfCircle CenterX=-36.5 CenterY=42 CenterZ=0 NormalX=0 NormalY=0 NormalZ=1 AngleXU=0 Radius=3 StartAngle=-9e-16 EndAngle=1.5708
    g11: GeomPoint [constr] X=-33.5 Y=45 Z=0
  constraints (32):
    c: Coincident(g1,g2)
    c: Horizontal(g0)
    c: Horizontal(g2)
    c: Vertical(g1)
    c: Vertical(g3)
    c: PointOnObject(g5,g0)
    c: PointOnObject(g5,g1)
    c: Tangent(g0,g4) = -1.5708
    c: Tangent(g1,g4) = -1.5708
    c: Horizontal(g6)
    c: Coincident(g6,g7)
    c: Vertical(g7)
    c: Coincident(g2,g7)
    c: DistanceX(g2,g2) = 6
    c: DistanceY(g6,g11) = 12
    c: Radius(g4) = 6
    c: Coincident(g9,g8)
    c: Radius(g8) = 3
    c: Perpendicular(g8,g9)
    c: Vertical(g9)
    c: Coincident(g6,g9)
    c: Tangent(g3,g8) = 1.5708
    c: DistanceY(g9,g9) = 3
    c: DistanceX(g6) = -30.5
    c: DistanceY(g6) = 33
    c: DistanceX(g6,g6) = 12
    c: DistanceY(g7,g7) = 5
    c: PointOnObject(g11,g0)
    c: PointOnObject(g11,g3)
    c: Tangent(g0,g10) = -1.5708
    c: Tangent(g3,g10) = -1.5708
    c: Radius(g10) = 3
FEATURE [Sketcher::SketchObject] Sketch052
  ArcFitTolerance = 1e-06
  AttachmentSupport = -> [XY_Plane012]
  FullyConstrained = true
  MakeInternals = false
  MapMode = 5
  sketch-geometry (1):
    g0: Circle CenterX=-42 CenterY=38.5 CenterZ=0 NormalX=0 NormalY=0 NormalZ=1 AngleXU=0 Radius=2.8
  constraints (3):
    c: Diameter(g0) = 5.6
    c: DistanceY(g0) = 38.5
    c: DistanceX(g0) = -42
FEATURE [Sketcher::SketchObject] Sketch060
  ArcFitTolerance = 1e-06
  AttachmentOffset = pos=(0,0,-10) rot=(0,0,1;0rad)
  AttachmentSupport = -> [Binder017]
  ExternalGeometry = -> [Binder017]
  FullyConstrained = false
  MakeInternals = false
  MapMode = 5
  Placement = pos=(-2.76627,-2.76627,6.77594) rot=(0.98311,-0.035247,0.17959;3.5228rad)
  sketch-geometry (13):
    g0: LineSegment StartX=67.277 StartY=-36.2124 StartZ=0 EndX=69.152 EndY=-38.3775 EndZ=0
    g1: LineSegment StartX=69.152 StartY=-38.3775 StartZ=0 EndX=63.7093 EndY=-43.091 EndZ=0
    g2: LineSegment StartX=63.7093 StartY=-43.091 StartZ=0 EndX=65.3132 EndY=-44.9431 EndZ=0
    g3: LineSegment StartX=65.3132 StartY=-44.9431 StartZ=0 EndX=32.1658 EndY=-73.6496 EndZ=0
    g4: LineSegment StartX=32.1658 StartY=-73.6496 StartZ=0 EndX=30.5619 EndY=-71.7976 EndZ=0
    g5: LineSegment StartX=30.5619 StartY=-71.7976 StartZ=0 EndX=23.4939 EndY=-77.9186 EndZ=0
    g6: LineSegment StartX=23.4939 StartY=-77.9186 StartZ=0 EndX=22.6035 EndY=-76.8904 EndZ=0
    g7: LineSegment StartX=22.6035 StartY=-76.8904 StartZ=0 EndX=18.3381 EndY=-65.7167 EndZ=0
    g8: LineSegment StartX=18.3381 StartY=-65.7167 StartZ=0 EndX=34.7325 EndY=-54.7567 EndZ=0
    g9: LineSegment StartX=34.7325 StartY=-54.7567 StartZ=0 EndX=48.8345 EndY=-42.5448 EndZ=0
    g10: LineSegment StartX=48.8345 StartY=-42.5448 StartZ=0 EndX=58.5174 EndY=-31.3336 EndZ=0
    g11: LineSegment StartX=58.5174 StartY=-31.3336 StartZ=0 EndX=67.277 EndY=-36.2124 EndZ=0
    g12: LineSegment [constr] StartX=19.9771 StartY=-73.8577 StartZ=0 EndX=22.6035 EndY=-76.8904 EndZ=0
  constraints (23):
    c: Coincident(g0,g-4)
    c: Coincident(g0,g-5)
    c: Coincident(g0,g1)
    c: Coincident(g1,g-6)
    c: Coincident(g1,g2)
    c: Coincident(g2,g-7)
    c: Coincident(g2,g3)
    c: Coincident(g3,g-8)
    c: Coincident(g3,g4)
    c: Coincident(g4,g-9)
    c: Coincident(g4,g5)
    c: Coincident(g5,g-10)
    c: Coincident(g5,g6)
    c: Coincident(g7,g8)
    c: Coincident(g8,g9)
    c: Coincident(g9,g10)
    c: Coincident(g10,g11)
    c: Coincident(g11,g0)
    c: Angle(g11,g0) = 2.7927
    c: Angle(g6,g7) = 2.79253
    c: Coincident(g7,g6)
    c: Coincident(g12,g-3)
    c: Tangent(g12,g6) = 1.5708
FEATURE [PartDesign::AdditiveLoft] AdditiveLoft002
  BaseFeature = -> Pad022
  Closed = false
  Profile = -> Sketch059
  Refine = true
  Ruled = false
  Sections = -> [Sketch060]
  Suppressed = false
FEATURE [Sketcher::SketchObject] Sketch061
  ArcFitTolerance = 1e-06
  AttachmentSupport = -> [Binder040]
  ExternalGeometry = -> [Binder040]
  FullyConstrained = false
  MakeInternals = false
  MapMode = 5
  Placement = pos=(0.769267,-0.769267,-1.88431) rot=(0.98311,0.035247,0.179591;2.76038rad)
  sketch-geometry (13):
    g0: LineSegment StartX=26.23 StartY=71.7602 StartZ=0 EndX=28.105 EndY=73.9253 EndZ=0
    g1: LineSegment StartX=28.105 StartY=73.9253 StartZ=0 EndX=33.5477 EndY=69.2118 EndZ=0
    g2: LineSegment StartX=33.5477 StartY=69.2118 StartZ=0 EndX=35.1516 EndY=71.0638 EndZ=0
    g3: LineSegment StartX=35.1516 StartY=71.0638 StartZ=0 EndX=68.2991 EndY=42.3572 EndZ=0
    g4: LineSegment StartX=68.2991 StartY=42.3572 StartZ=0 EndX=66.6952 EndY=40.5052 EndZ=0
    g5: LineSegment StartX=66.6952 StartY=40.5052 StartZ=0 EndX=73.7631 EndY=34.3842 EndZ=0
    g6: LineSegment StartX=73.7631 StartY=34.3842 StartZ=0 EndX=70.2463 EndY=30.3233 EndZ=0
    g7: LineSegment StartX=70.2463 StartY=30.3233 StartZ=0 EndX=53.4637 EndY=20.9797 EndZ=0
    g8: LineSegment StartX=53.4637 StartY=20.9797 StartZ=0 EndX=50.5782 EndY=35.2097 EndZ=0
    g9: LineSegment StartX=50.5782 StartY=35.2097 StartZ=0 EndX=42.4985 EndY=45.139 EndZ=0
    g10: LineSegment StartX=42.4985 StartY=45.139 StartZ=0 EndX=29.0647 EndY=52.6347 EndZ=0
    g11: LineSegment StartX=29.0647 StartY=52.6347 StartZ=0 EndX=19.2336 EndY=53.4321 EndZ=0
    g12: LineSegment StartX=19.2336 StartY=53.4321 StartZ=0 EndX=26.23 EndY=71.7602 EndZ=0
  constraints (23):
    c: Coincident(g0,g-3)
    c: Coincident(g0,g-4)
    c: Coincident(g0,g1)
    c: Coincident(g1,g-5)
    c: Coincident(g1,g2)
    c: Coincident(g2,g-6)
    c: Coincident(g2,g3)
    c: Coincident(g3,g-7)
    c: Coincident(g3,g4)
    c: Coincident(g4,g-8)
    c: Coincident(g4,g5)
    c: Coincident(g5,g-9)
    c: Coincident(g5,g6)
    c: Coincident(g6,g-10)
    c: Coincident(g6,g7)
    c: Coincident(g7,g8)
    c: Coincident(g8,g9)
    c: Coincident(g9,g10)
    c: Coincident(g10,g11)
    c: Coincident(g11,g12)
    c: Coincident(g12,g0)
    c: Angle(g6,g7) = 2.79253
    c: Angle(g12,g0) = 2.79253
FEATURE [Sketcher::SketchObject] Sketch062
  ArcFitTolerance = 1e-06
  AttachmentOffset = pos=(0,0,-10) rot=(0,0,1;0rad)
  AttachmentSupport = -> [Binder040]
  ExternalGeometry = -> [Binder040]
  FullyConstrained = false
  MakeInternals = false
  MapMode = 5
  Placement = pos=(-2.76627,2.76627,6.77594) rot=(0.98311,0.035247,0.179591;2.76038rad)
  sketch-geometry (13):
    g0: LineSegment StartX=26.23 StartY=71.7602 StartZ=0 EndX=28.105 EndY=73.9253 EndZ=0
    g1: LineSegment StartX=28.105 StartY=73.9253 StartZ=0 EndX=33.5477 EndY=69.2118 EndZ=0
    g2: LineSegment StartX=33.5477 StartY=69.2118 StartZ=0 EndX=35.1516 EndY=71.0638 EndZ=0
    g3: LineSegment StartX=35.1516 StartY=71.0638 StartZ=0 EndX=68.2991 EndY=42.3572 EndZ=0
    g4: LineSegment StartX=68.2991 StartY=42.3572 StartZ=0 EndX=66.6952 EndY=40.5052 EndZ=0
    g5: LineSegment StartX=66.6952 StartY=40.5052 StartZ=0 EndX=73.7631 EndY=34.3842 EndZ=0
    g6: LineSegment StartX=73.7631 StartY=34.3842 StartZ=0 EndX=70.2463 EndY=30.3233 EndZ=0
    g7: LineSegment StartX=70.2463 StartY=30.3233 StartZ=0 EndX=58.016 EndY=23.5141 EndZ=0
    g8: LineSegment StartX=58.016 StartY=23.5141 StartZ=0 EndX=53.2451 EndY=38.3156 EndZ=0
    g9: LineSegment StartX=53.2451 StartY=38.3156 StartZ=0 EndX=44.7307 EndY=48.1473 EndZ=0
    g10: LineSegment StartX=44.7307 StartY=48.1473 StartZ=0 EndX=31.3681 EndY=55.9125 EndZ=0
    g11: LineSegment StartX=31.3681 StartY=55.9125 StartZ=0 EndX=21.7527 EndY=60.0312 EndZ=0
    g12: LineSegment StartX=21.7527 StartY=60.0312 StartZ=0 EndX=26.23 EndY=71.7602 EndZ=0
  constraints (23):
    c: Coincident(g0,g-3)
    c: Coincident(g0,g-4)
    c: Coincident(g0,g1)
    c: Coincident(g1,g-5)
    c: Coincident(g1,g2)
    c: Coincident(g2,g-6)
    c: Coincident(g2,g3)
    c: Coincident(g3,g-7)
    c: Coincident(g3,g4)
    c: Coincident(g4,g-8)
    c: Coincident(g4,g5)
    c: Coincident(g5,g-9)
    c: Coincident(g5,g6)
    c: Coincident(g6,g-10)
    c: Coincident(g6,g7)
    c: Coincident(g7,g8)
    c: Coincident(g8,g9)
    c: Coincident(g9,g10)
    c: Coincident(g10,g11)
    c: Coincident(g11,g12)
    c: Coincident(g12,g0)
    c: Angle(g12,g0) = 2.79253
    c: Angle(g6,g7) = 2.79253
FEATURE [PartDesign::AdditiveLoft] AdditiveLoft003
  BaseFeature = -> AdditiveLoft002
  Closed = false
  Profile = -> Sketch061
  Refine = true
  Ruled = false
  Sections = -> [Sketch062]
  Suppressed = false
FEATURE [PartDesign::PolarPattern] PolarPattern009
  Angle = 360
  Axis = -> Z_Axis012
  BaseFeature = -> AdditiveLoft003
  Mode = 0
  Occurrences = 2
  Offset = 120
  Originals = -> [AdditiveLoft002,AdditiveLoft003]
  Refine = true
  Suppressed = false
  TransformMode = 0
FEATURE [PartDesign::Boolean] Boolean002  label="BooleanUSB"
  BaseFeature = -> PolarPattern009
  Group = -> [Binder030]
  Refine = true
  Suppressed = false
  Type = 1
  UsePlacement = true
FEATURE [PartDesign::Boolean] Boolean003  label="BooleanAkku"
  BaseFeature = -> Boolean002
  Group = -> [Binder021]
  Refine = true
  Suppressed = false
  Type = 1
  UsePlacement = true
FEATURE [PartDesign::Boolean] Boolean004  label="BooleanESP"
  BaseFeature = -> Boolean003
  Group = -> [Binder022]
  Refine = true
  Suppressed = false
  Type = 1
  UsePlacement = true
FEATURE [PartDesign::Boolean] Boolean005  label="BooleanLC"
  BaseFeature = -> Boolean004
  Group = -> [Binder023]
  Refine = true
  Suppressed = false
  Type = 1
  UsePlacement = true
FEATURE [PartDesign::Boolean] Boolean006  label="BooleanEnc"
  BaseFeature = -> Boolean005
  Group = -> [Binder024]
  Refine = true
  Suppressed = false
  Type = 1
  UsePlacement = true
FEATURE [PartDesign::Boolean] Boolean007  label="BooleanEnc2"
  BaseFeature = -> Boolean006
  Group = -> [Binder026]
  Refine = true
  Suppressed = false
  Type = 1
  UsePlacement = true
FEATURE [PartDesign::Pad] Pad027  label="PadScrewPad"
  BaseFeature = -> Boolean007
  Direction = (0,0,1)
  Length = 10
  Length2 = 10
  Profile = -> Sketch051
  ReferenceAxis = -> Sketch051 [N_Axis]
  Refine = true
  Suppressed = false
  Type = 0
FEATURE [PartDesign::Pocket] Pocket009  label="PocketScrew"
  BaseFeature = -> Pad027
  Direction = (0,0,-1)
  Length = 9
  Length2 = 5
  Profile = -> Sketch052
  ReferenceAxis = -> Sketch052 [N_Axis]
  Refine = true
  Reversed = true
  Suppressed = false
  Type = 0
FEATURE [PartDesign::MultiTransform] MultiTransform001  label="MultiTransformScrews"
  BaseFeature = -> Pocket009
  Originals = -> [Pad027,Pocket009]
  Refine = true
  Suppressed = false
  TransformMode = 0
  Transformations = -> [Mirrored,Mirrored001]
FEATURE [PartDesign::Body] Body012  label="Inner"
  AllowCompound = true
  BaseFeature = -> Cut002
  Group = -> [BaseFeature,Sketch024,Sketch025,AdditiveLoft,Sketch027,Sketch028,Pocket003,Sketch029,Sketch030,Pad019,Sketch031,Pad020,Sketch032,Pad021,Binder016,Sketch033,Pad022,Binder017,Sketch061,Sketch062,AdditiveLoft002,AdditiveLoft003,Binder018,Sketch060,PolarPattern009,Boolean002,Boolean003,Boolean004,Boolean005,Boolean006,Boolean007,Sketch042,Sketch051,Pad027,Sketch052,Pocket009,MultiTransform001,+6 more]
  Origin = -> Origin012
  Tip = -> Boolean016
COMPONENT P4 — recipe-attached ("base_button_cut", modeled in this document).
Construction recipe (the document's own serialized feature program — sketch geometry with constraints, then the solid features built on it; lengths are millimeters unless a unit is written):

FEATURE [PartDesign::SubShapeBinder] Binder025
  BindCopyOnChange = 0
  BindMode = 0
  ClaimChildren = false
  Context = -> Body013 [Binder025.]
  Fuse = false
  MakeFace = true
  OffsetFill = false
  OffsetIntersection = false
  OffsetJoinType = 0
  OffsetOpenResult = false
  PartialLoad = false
  Refine = true
  Relative = true
  Support = -> [Link006[Pad012.Edge49]]
  _Version = 2
FEATURE [Sketcher::SketchObject] Sketch036
  ArcFitTolerance = 1e-06
  AttachmentOffset = pos=(0,0,-2) rot=(0,0,1;0rad)
  AttachmentSupport = -> [Binder025]
  ExternalGeometry = -> [Binder025]
  FullyConstrained = true
  MakeInternals = false
  MapMode = 5
  Placement = pos=(2.76483e-06,-56.8113,32.8) rot=(0,0.866025,0.5;3.14159rad)
  sketch-geometry (1):
    g0: Circle CenterX=4.85576e-06 CenterY=-20.5703 CenterZ=0 NormalX=0 NormalY=0 NormalZ=1 AngleXU=0 Radius=12.75
  constraints (2):
    c: Diameter(g0) = 25.5
    c: Coincident(g0,g-3)
FEATURE [PartDesign::Pad] Pad025
  Direction = (-4.21469e-08,0.866026,-0.5)
  Length = 30
  Length2 = 10
  Profile = -> Sketch036
  ReferenceAxis = -> Sketch036 [N_Axis]
  Refine = true
  Reversed = true
  Suppressed = false
  Type = 0
FEATURE [PartDesign::Body] Body013  label="base_button_cut"
  AllowCompound = false
  Group = -> [Binder025,Sketch036,Pad025]
  Origin = -> Origin013
  Tip = -> Pad025
COMPONENT P5 — recipe-attached ("Outer", modeled in this document).
Construction recipe (the document's own serialized feature program — sketch geometry with constraints, then the solid features built on it; lengths are millimeters unless a unit is written):

FEATURE [PartDesign::FeatureBase] BaseFeature001
  BaseFeature = -> CompoundFilter
  Suppressed = false
FEATURE [PartDesign::Boolean] Boolean009  label="BooleanEncoder"
  BaseFeature = -> BaseFeature001
  Group = -> [Binder028]
  Refine = true
  Suppressed = false
  Type = 1
  UsePlacement = true
FEATURE [PartDesign::Boolean] Boolean012  label="BooleanSwitch"
  BaseFeature = -> Boolean009
  Group = -> [Binder032]
  Refine = true
  Suppressed = false
  Type = 1
  UsePlacement = true
FEATURE [Sketcher::SketchObject] Sketch079
  ArcFitTolerance = 1e-06
  AttachmentSupport = -> [YZ_Plane014]
  FullyConstrained = true
  MakeInternals = false
  MapMode = 5
  Placement = pos=(0,0,0) rot=(0.57735,-0.57735,-0.57735;2.0944rad)
  sketch-geometry (8):
    g0: LineSegment StartX=92.9 StartY=0 StartZ=0 EndX=92.9 EndY=1.95 EndZ=0
    g1: LineSegment StartX=92.9 StartY=1.95 StartZ=0 EndX=92.0609 EndY=2.95 EndZ=0
    g2: LineSegment StartX=90.1891 StartY=2.95 StartZ=0 EndX=89.35 EndY=1.95 EndZ=0
    g3: LineSegment StartX=89.35 StartY=1.95 StartZ=0 EndX=89.35 EndY=1.75 EndZ=0
    g4: LineSegment StartX=89.35 StartY=1.75 StartZ=0 EndX=89.85 EndY=1.25 EndZ=0
    g5: LineSegment StartX=89.85 StartY=1.25 StartZ=0 EndX=89.85 EndY=0 EndZ=0
    g6: LineSegment StartX=89.85 StartY=0 StartZ=0 EndX=92.9 EndY=0 EndZ=0
    g7: LineSegment StartX=90.1891 StartY=2.95 StartZ=0 EndX=92.0609 EndY=2.95 EndZ=0
  constraints (24):
    c: Vertical(g0)
    c: Coincident(g0,g1)
    c: Coincident(g2,g3)
    c: Coincident(g3,g4)
    c: Coincident(g4,g5)
    c: PointOnObject(g5,g-1)
    c: Vertical(g5)
    c: Coincident(g5,g6)
    c: Coincident(g6,g0)
    c: Horizontal(g6)
    c: DistanceX(g5) = 89.85
    c: DistanceX(g4,g4) = 0.5
    c: Vertical(g3)
    c: Angle(g3,g2) = 2.44346
    c: Angle(g1,g0) = 2.44346
    c: DistanceX(g6,g6) = 3.05
    c: Coincident(g7,g2)
    c: Coincident(g7,g1)
    c: Horizontal(g7)
    c: DistanceY(g2,g2) = 1
    c: Horizontal(g0,g2)
    c: DistanceY(g3) = 1.75
    c: Angle(g4,g3) = 2.35619
    c: DistanceY(g3,g3) = 0.2
FEATURE [PartDesign::Groove] Groove
  Angle = 348
  Angle2 = 60
  Axis = (0,0,1)
  Base = (0,0,0)
  BaseFeature = -> Boolean012
  Midplane = true
  Profile = -> Sketch079
  ReferenceAxis = -> Sketch079 [V_Axis]
  Refine = true
  Suppressed = false
  Type = 0
FEATURE [PartDesign::Boolean] Boolean017  label="BooleanBrackets"
  BaseFeature = -> Groove
  Group = -> [Binder038]
  Refine = true
  Suppressed = false
  Type = 1
  UsePlacement = true
FEATURE [PartDesign::Boolean] Boolean018  label="BooleanESP001"
  BaseFeature = -> Boolean017
  Group = -> [Binder042]
  Refine = true
  Suppressed = false
  Type = 1
  UsePlacement = true
FEATURE [PartDesign::SubShapeBinder] Binder053  label="BinderESPBottom"
  BindCopyOnChange = 0
  BindMode = 0
  ClaimChildren = false
  Context = -> Body014 [Binder053.]
  Fuse = false
  MakeFace = true
  OffsetFill = false
  OffsetIntersection = false
  OffsetJoinType = 0
  OffsetOpenResult = false
  PartialLoad = false
  Refine = true
  Relative = true
  Support = -> [Link005[Pad032.Face3]]
  _Version = 2
FEATURE [PartDesign::Pocket] Pocket012  label="PocketEspExtra"
  BaseFeature = -> Boolean018
  Direction = (-0.3,0,-1)
  Length = 10
  Length2 = 5
  Profile = -> Binder053
  Refine = true
  Suppressed = false
  TaperAngle = 14
  Type = 0
  UseCustomVector = true
FEATURE [PartDesign::Boolean] Boolean019  label="BooleanSkin"
  BaseFeature = -> Pocket012
  Group = -> [Binder051]
  Refine = true
  Suppressed = false
  Type = 1
  UsePlacement = true
FEATURE [Sketcher::SketchObject] Sketch086
  ArcFitTolerance = 1e-06
  AttachmentSupport = -> [XZ_Plane014]
  FullyConstrained = false
  MakeInternals = false
  MapMode = 5
  Placement = pos=(0,0,0) rot=(1,0,0;1.5708rad)
  sketch-geometry (5):
    g0: LineSegment StartX=-68.7883 StartY=35 StartZ=0 EndX=-73.869 EndY=35 EndZ=0
    g1: LineSegment StartX=-73.869 StartY=35 StartZ=0 EndX=-87.7254 EndY=11 EndZ=0
    g2: LineSegment StartX=-87.7254 StartY=11 StartZ=0 EndX=-85.185 EndY=6.6 EndZ=0
    g3: LineSegment StartX=-85.185 StartY=6.6 StartZ=0 EndX=-68.7883 EndY=35 EndZ=0
    g4: LineSegment [constr] StartX=-95 StartY=0 StartZ=0 EndX=-74.3753 EndY=35.7229 EndZ=0
  constraints (15):
    c: Coincident(g0,g1)
    c: Coincident(g1,g2)
    c: Coincident(g2,g3)
    c: Coincident(g3,g0)
    c: Angle(g-1,g3) = 1.0472
    c: Parallel(g1,g3)
    c: Angle(g1,g0) = 2.0944
    c: Angle(g2,g1) = 2.0944
    c: DistanceY(g1) = 11
    c: DistanceY(g0) = 35
    c: PointOnObject(g4,g-1)
    c: DistanceX(g4) = -95
    c: Angle(g4,g-1) = 2.0944
    c: Distance(g1,g4) = 0.8
    c: Distance(g3,g4) = 5.2
FEATURE [PartDesign::Groove] Groove001
  Angle = 32
  Angle2 = 60
  Axis = (0,2e-16,1)
  Base = (0,0,0)
  BaseFeature = -> Boolean019
  Midplane = true
  Profile = -> Sketch086
  ReferenceAxis = -> Sketch086 [V_Axis]
  Refine = true
  Reversed = true
  Suppressed = false
  Type = 0
FEATURE [PartDesign::Boolean] Boolean008  label="BooleanUSB001"
  BaseFeature = -> Groove001
  Group = -> [Binder027]
  Refine = true
  Suppressed = false
  Type = 1
  UsePlacement = true
FEATURE [PartDesign::Chamfer] Chamfer  label="ChamferDisplays"
  Angle = 45
  Base = -> Boolean008 [Edge590,Edge564,Edge536,Edge502]
  BaseFeature = -> Boolean008
  ChamferType = 0
  FlipDirection = false
  Refine = true
  Size = 1.5
  Size2 = 1
  SupportTransform = false
  Suppressed = false
  UseAllEdges = false
FEATURE [PartDesign::Chamfer] Chamfer003  label="ChamferKnob"
  Angle = 45
  Base = -> Chamfer [Edge514]
  BaseFeature = -> Chamfer
  ChamferType = 0
  FlipDirection = false
  Refine = true
  Size = 1
  Size2 = 1
  SupportTransform = false
  Suppressed = false
  UseAllEdges = false
FEATURE [PartDesign::Boolean] Boolean020  label="BooleanFet"
  BaseFeature = -> Chamfer003
  Group = -> [Binder052]
  Refine = true
  Suppressed = false
  Type = 1
  UsePlacement = true
FEATURE [PartDesign::Body] Body014  label="Outer"
  AllowCompound = true
  BaseFeature = -> CompoundFilter
  Group = -> [BaseFeature001,Boolean009,Boolean012,Sketch079,Groove,Boolean017,Boolean018,Binder053,Pocket012,Boolean019,Sketch086,Groove001,Boolean008,Chamfer,Chamfer003,Boolean020]
  Origin = -> Origin014
  Tip = -> Boolean020
COMPONENT P6 — recipe-attached ("Distance", modeled in this document).
Construction recipe (the document's own serialized feature program — sketch geometry with constraints, then the solid features built on it; lengths are millimeters unless a unit is written):

FEATURE [Sketcher::SketchObject] Sketch045
  ArcFitTolerance = 1e-06
  AttachmentOffset = pos=(0,0,22.7) rot=(0,0,1;0rad)
  AttachmentSupport = -> [XY_Plane015]
  FullyConstrained = true
  MakeInternals = false
  MapMode = 5
  Placement = pos=(0,0,22.7) rot=(0,0,1;0rad)
  sketch-geometry (4):
    g0: LineSegment StartX=-10.5 StartY=6.4 StartZ=0 EndX=-10.5 EndY=-6.4 EndZ=0
    g1: LineSegment StartX=-10.5 StartY=-6.4 StartZ=0 EndX=10.5 EndY=-6.4 EndZ=0
    g2: LineSegment StartX=10.5 StartY=-6.4 StartZ=0 EndX=10.5 EndY=6.4 EndZ=0
    g3: LineSegment StartX=10.5 StartY=6.4 StartZ=0 EndX=-10.5 EndY=6.4 EndZ=0
  constraints (11):
    c: Coincident(g0,g1)
    c: Coincident(g1,g2)
    c: Coincident(g2,g3)
    c: Coincident(g3,g0)
    c: Vertical(g0)
    c: Vertical(g2)
    c: Horizontal(g1)
    c: Horizontal(g3)
    c: Symmetric(g0,g2,g-1)
    c: DistanceX(g1,g1) = 21
    c: DistanceY(g2,g2) = 12.8
FEATURE [Sketcher::SketchObject] Sketch046
  ArcFitTolerance = 1e-06
  AttachmentOffset = pos=(0,0,34) rot=(0,0,1;0rad)
  AttachmentSupport = -> [XY_Plane015]
  FullyConstrained = true
  MakeInternals = false
  MapMode = 5
  Placement = pos=(0,0,34) rot=(0,0,1;0rad)
  sketch-geometry (1):
    g0: Circle CenterX=0 CenterY=0 CenterZ=0 NormalX=0 NormalY=0 NormalZ=1 AngleXU=0 Radius=10
  constraints (2):
    c: Diameter(g0) = 20
    c: Coincident(g0,g-1)
FEATURE [PartDesign::AdditiveLoft] AdditiveLoft001
  Closed = false
  Profile = -> Sketch045
  Refine = true
  Ruled = false
  Sections = -> [Sketch046]
  Suppressed = false
FEATURE [Sketcher::SketchObject] Sketch047
  ArcFitTolerance = 1e-06
  AttachmentSupport = -> [XY_Plane015]
  FullyConstrained = true
  MakeInternals = false
  MapMode = 5
  sketch-geometry (2):
    g0: Circle CenterX=-5 CenterY=0 CenterZ=0 NormalX=0 NormalY=0 NormalZ=1 AngleXU=0 Radius=2.25
    g1: Circle CenterX=5 CenterY=0 CenterZ=0 NormalX=0 NormalY=0 NormalZ=1 AngleXU=0 Radius=2.25
  constraints (6):
    c: Diameter(g0) = 4.5
    c: PointOnObject(g0,g-1)
    c: PointOnObject(g1,g-1)
    c: Equal(g1,g0)
    c: DistanceX(g1) = 5
    c: DistanceX(g0) = -5
FEATURE [PartDesign::Pocket] Pocket007
  BaseFeature = -> AdditiveLoft001
  Direction = (0,0,-1)
  Length = 5
  Length2 = 5
  Midplane = true
  Profile = -> Sketch047
  ReferenceAxis = -> Sketch047 [N_Axis]
  Refine = true
  Suppressed = false
  Type = 1
FEATURE [PartDesign::Body] Body015  label="Distance"
  AllowCompound = false
  Group = -> [Sketch045,Sketch046,AdditiveLoft001,Sketch047,Pocket007]
  Origin = -> Origin015
  Tip = -> Pocket007
COMPONENT P7 — recipe-attached ("Top", modeled in this document).
Construction recipe (the document's own serialized feature program — sketch geometry with constraints, then the solid features built on it; lengths are millimeters unless a unit is written):

FEATURE [Sketcher::SketchObject] Sketch089
  ArcFitTolerance = 1e-06
  AttachmentSupport = -> [XZ_Plane017]
  FullyConstrained = true
  MakeInternals = false
  MapMode = 5
  Placement = pos=(0,0,0) rot=(1,0,0;1.5708rad)
  sketch-geometry (11):
    g0: LineSegment StartX=0 StartY=34 StartZ=0 EndX=36 EndY=34 EndZ=0
    g1: LineSegment StartX=36 StartY=34 StartZ=0 EndX=36 EndY=41.4 EndZ=0
    g2: LineSegment StartX=43.2 StartY=41.4 StartZ=0 EndX=43.2 EndY=34 EndZ=0
    g3: LineSegment StartX=43.2 StartY=34 StartZ=0 EndX=44.2 EndY=34 EndZ=0
    g4: LineSegment StartX=48 StartY=45 StartZ=0 EndX=44 EndY=45 EndZ=0
    g5: LineSegment StartX=44 StartY=45 StartZ=0 EndX=43.2 EndY=42 EndZ=0
    g6: LineSegment StartX=43.2 StartY=42 StartZ=0 EndX=0 EndY=42 EndZ=0
    g7: LineSegment StartX=0 StartY=42 StartZ=0 EndX=0 EndY=34 EndZ=0
    g8: LineSegment StartX=36 StartY=41.4 StartZ=0 EndX=43.2 EndY=41.4 EndZ=0
    g9: LineSegment StartX=44.2 StartY=34 StartZ=0 EndX=48 EndY=41.4 EndZ=0
    g10: LineSegment StartX=48 StartY=41.4 StartZ=0 EndX=48 EndY=45 EndZ=0
  constraints (33):
    c: Horizontal(g0)
    c: Coincident(g0,g1)
    c: Vertical(g1)
    c: Vertical(g2)
    c: Coincident(g2,g3)
    c: Horizontal(g3)
    c: Coincident(g4,g5)
    c: Coincident(g5,g6)
    c: PointOnObject(g6,g-2)
    c: Horizontal(g6)
    c: Coincident(g6,g7)
    c: Vertical(g7)
    c: DistanceX(g0) = 36
    c: DistanceX(g2) = 43.2
    c: DistanceY(g4) = 45
    c: Horizontal(g4)
    c: DistanceY(g5,g5) = 3
    c: Horizontal(g2,g0)
    c: Horizontal(g2,g1)
    c: Coincident(g8,g1)
    c: Coincident(g8,g2)
    c: DistanceX(g4,g4) = 4
    c: DistanceY(g2,g5) = 0.6
    c: Coincident(g0,g7)
    c: DistanceX(g4) = 48
    c: DistanceX(g3,g3) = 1
    c: Vertical(g5,g2)
    c: DistanceY(g2,g5) = 8
    c: Coincident(g3,g9)
    c: Coincident(g9,g10)
    c: Coincident(g10,g4)
    c: Vertical(g10)
    c: Horizontal(g9,g2)
FEATURE [PartDesign::Revolution] Revolution011
  Angle = 360
  Angle2 = 60
  Axis = (0,2e-16,1)
  Base = (0,0,0)
  Placement = pos=(0,0,0) rot=(1,0,0;1.5708rad)
  Profile = -> Sketch089
  ReferenceAxis = -> Sketch089 [V_Axis]
  Refine = true
  Reversed = true
  Suppressed = false
  Type = 0
FEATURE [Sketcher::SketchObject] Sketch055
  ArcFitTolerance = 1e-06
  AttachmentSupport = -> [Revolution011]
  FullyConstrained = true
  MakeInternals = false
  MapMode = 5
  Placement = pos=(0,1.85e-14,42) rot=(0,0,1;3.14159rad)
  sketch-geometry (2):
    g0: Circle CenterX=5 CenterY=0 CenterZ=0 NormalX=0 NormalY=0 NormalZ=1 AngleXU=0 Radius=2.25
    g1: Circle CenterX=-5 CenterY=0 CenterZ=0 NormalX=0 NormalY=0 NormalZ=1 AngleXU=0 Radius=2.25
  constraints (6):
    c: PointOnObject(g0,g-1)
    c: PointOnObject(g1,g-1)
    c: Equal(g1,g0)
    c: Diameter(g1) = 4.5
    c: DistanceX(g0) = 5
    c: DistanceX(g1) = -5
FEATURE [Sketcher::SketchObject] Sketch091
  ArcFitTolerance = 1e-06
  AttachmentOffset = pos=(0,0,42) rot=(0,0,1;0.1309rad)
  AttachmentSupport = -> [XY_Plane017]
  FullyConstrained = true
  MakeInternals = false
  MapMode = 5
  Placement = pos=(0,0,42) rot=(0,0,1;0.1309rad)
  sketch-geometry (4):
    g0: LineSegment StartX=0 StartY=0.8 StartZ=0 EndX=0 EndY=-0.8 EndZ=0
    g1: LineSegment StartX=0 StartY=-0.8 StartZ=0 EndX=44.5 EndY=-0.8 EndZ=0
    g2: LineSegment StartX=44.5 StartY=-0.8 StartZ=0 EndX=44.5 EndY=0.8 EndZ=0
    g3: LineSegment StartX=44.5 StartY=0.8 StartZ=0 EndX=0 EndY=0.8 EndZ=0
  constraints (11):
    c: Coincident(g0,g1)
    c: Coincident(g1,g2)
    c: Coincident(g2,g3)
    c: Coincident(g3,g0)
    c: Vertical(g0)
    c: Horizontal(g1)
    c: Horizontal(g3)
    c: PointOnObject(g0,g-2)
    c: DistanceX(g2) = 44.5
    c: DistanceY(g2,g2) = 1.6
    c: Symmetric(g1,g2,g-1)
FEATURE [PartDesign::Pad] Pad034
  BaseFeature = -> Revolution011
  Direction = (0,0,1)
  Length = 6
  Length2 = 10
  Placement = pos=(0,0,0) rot=(1,0,0;1.5708rad)
  Profile = -> Sketch091
  ReferenceAxis = -> Sketch091 [N_Axis]
  Refine = true
  Reversed = true
  Suppressed = false
  Type = 0
FEATURE [PartDesign::PolarPattern] PolarPattern017
  Angle = 360
  Axis = -> Sketch091 [N_Axis]
  BaseFeature = -> Pad034
  Mode = 0
  Occurrences = 24
  Offset = 120
  Originals = -> [Pad034]
  Placement = pos=(0,0,0) rot=(1,0,0;1.5708rad)
  Refine = true
  Suppressed = false
  TransformMode = 0
FEATURE [PartDesign::Hole] Hole001
  BaseFeature = -> PolarPattern017
  CustomThreadClearance = 0
  Depth = 25
  DepthType = 0
  Diameter = 4.5
  DrillForDepth = false
  DrillPoint = 1
  DrillPointAngle = 118
  HoleCutCountersinkAngle = 90
  HoleCutCustomValues = false
  HoleCutDepth = 4.4
  HoleCutDiameter = 7
  HoleCutType = 1
  ModelThread = false
  Placement = pos=(0,0,0) rot=(1,0,0;1.5708rad)
  Profile = -> Sketch055
  Refine = true
  Suppressed = false
  Tapered = false
  TaperedAngle = 90
  ThreadClass = 0
  ThreadDepth = 25
  ThreadDepthType = 0
  ThreadDirection = 0
  ThreadFit = 0
  ThreadSize = 11
  ThreadType = 1
  Threaded = false
  UseCustomThreadClearance = false
FEATURE [PartDesign::Body] Body017  label="Top"
  AllowCompound = false
  Group = -> [Revolution011,Sketch055,Sketch089,Sketch091,Pad034,PolarPattern017,Hole001]
  Origin = -> Origin017
  Tip = -> Hole001
COMPONENT P8 — recipe-attached ("Displaybrackets", modeled in this document).
Construction recipe (the document's own serialized feature program — sketch geometry with constraints, then the solid features built on it; lengths are millimeters unless a unit is written):

FEATURE [Sketcher::SketchObject] Sketch056
  ArcFitTolerance = 1e-06
  AttachmentOffset = pos=(0,0,0) rot=(0,1,0;0.785398rad)
  AttachmentSupport = -> [XZ_Plane018]
  FullyConstrained = true
  MakeInternals = false
  MapMode = 5
  Placement = pos=(0,0,0) rot=(0.862856,0.357407,0.357407;1.71777rad)
  sketch-geometry (22):
    g0: LineSegment StartX=66.9852 StartY=13.8423 StartZ=0 EndX=53.4852 EndY=37.225 EndZ=0
    g1: ArcOfCircle CenterX=65.75 CenterY=32.1817 CenterZ=0 NormalX=0 NormalY=0 NormalZ=1 AngleXU=0 Radius=1.35 StartAngle=5.23599 EndAngle=8.37758
    g2: ArcOfCircle CenterX=66.875 CenterY=30.2332 CenterZ=0 NormalX=0 NormalY=0 NormalZ=1 AngleXU=0 Radius=0.9 StartAngle=2.0944 EndAngle=3.66519
    g3: LineSegment StartX=66.0956 StartY=29.7832 StartZ=0 EndX=78.0956 EndY=8.99856 EndZ=0
    g4: ArcOfCircle CenterX=78.875 CenterY=9.44856 CenterZ=0 NormalX=0 NormalY=0 NormalZ=1 AngleXU=0 Radius=0.9 StartAngle=3.66519 EndAngle=5.23599
    g5: ArcOfCircle CenterX=80 CenterY=7.5 CenterZ=0 NormalX=0 NormalY=0 NormalZ=1 AngleXU=0 Radius=1.35 StartAngle=5.23599 EndAngle=8.37758
    g6: ArcOfCircle CenterX=78.875 CenterY=9.44856 CenterZ=0 NormalX=0 NormalY=0 NormalZ=1 AngleXU=0 Radius=3.6 StartAngle=3.66519 EndAngle=5.23599
    g7: LineSegment StartX=75.7573 StartY=7.64856 StartZ=0 EndX=70.8823 EndY=16.0923 EndZ=0
    g8: ArcOfCircle CenterX=70.1029 CenterY=15.6423 CenterZ=0 NormalX=0 NormalY=0 NormalZ=1 AngleXU=0 Radius=0.9 StartAngle=0.523599 EndAngle=3.66519
    g9: LineSegment [constr] StartX=79.325 StartY=8.66913 StartZ=0 EndX=80.675 EndY=6.33087 EndZ=0
    g10: LineSegment [constr] StartX=75.7573 StartY=7.64856 StartZ=0 EndX=78.0956 EndY=8.99856 EndZ=0
    g11: ArcOfCircle CenterX=67.8529 CenterY=19.5394 CenterZ=0 NormalX=0 NormalY=0 NormalZ=1 AngleXU=0 Radius=0.9 StartAngle=3.66519 EndAngle=6.80678
    g12: LineSegment StartX=68.6323 StartY=19.9894 StartZ=0 EndX=63.7573 EndY=28.4332 EndZ=0
    g13: ArcOfCircle CenterX=66.875 CenterY=30.2332 CenterZ=0 NormalX=0 NormalY=0 NormalZ=1 AngleXU=0 Radius=3.6 StartAngle=2.0944 EndAngle=3.66519
    g14: LineSegment [constr] StartX=65.075 StartY=33.3509 StartZ=0 EndX=66.425 EndY=31.0126 EndZ=0
    g15: ArcOfCircle CenterX=68.1543 CenterY=14.5173 CenterZ=0 NormalX=0 NormalY=0 NormalZ=1 AngleXU=0 Radius=1.35 StartAngle=3.66519 EndAngle=6.80678
    g16: ArcOfCircle CenterX=54.6543 CenterY=37.9 CenterZ=0 NormalX=0 NormalY=0 NormalZ=1 AngleXU=0 Radius=1.35 StartAngle=0.523599 EndAngle=3.66519
    g17: LineSegment StartX=55.8235 StartY=38.575 StartZ=0 EndX=67.0735 EndY=19.0894 EndZ=0
    g18: LineSegment [constr] StartX=70.8823 StartY=16.0923 StartZ=0 EndX=69.3235 EndY=15.1923 EndZ=0
    g19: LineSegment [constr] StartX=68.6323 StartY=19.9894 StartZ=0 EndX=67.0735 EndY=19.0894 EndZ=0
    g20: LineSegment [constr] StartX=69.3235 StartY=15.1923 StartZ=0 EndX=66.9852 EndY=13.8423 EndZ=0
    g21: LineSegment [constr] StartX=53.4852 StartY=37.225 StartZ=0 EndX=55.8235 EndY=38.575 EndZ=0
  constraints (54):
    c: Tangent(g1,g2) = 1.5708
    c: Tangent(g2,g3) = -1.5708
    c: Tangent(g3,g4) = -1.5708
    c: Tangent(g4,g5) = 1.5708
    c: Tangent(g5,g6) = -1.5708
    c: Tangent(g7,g8) = -1.5708
    c: Equal(g5,g1)
    c: Equal(g4,g2)
    c: Tangent(g6,g7) = 1.5708
    c: Coincident(g9,g4)
    c: Coincident(g9,g5)
    c: Coincident(g4,g6)
    c: Radius(g8) = 0.9
    c: Angle(g0,g-1) = 1.0472
    c: Parallel(g3,g7)
    c: Equal(g2,g8)
    c: Coincident(g10,g6)
    c: Coincident(g10,g3)
    c: Perpendicular(g10,g9)
    c: Tangent(g11,g12) = -1.5708
    c: Tangent(g12,g13) = 1.5708
    c: Tangent(g13,g1) = -1.5708
    c: Coincident(g14,g1)
    c: Coincident(g14,g1)
    c: PointOnObject(g1,g14)
    c: Tangent(g7,g12)
    c: Equal(g8,g11)
    c: Equal(g7,g12)
    c: Parallel(g14,g3)
    c: Distance(g12,g2) = 2.7
    c: DistanceY(g5) = 7.5
    c: DistanceX(g5) = 80
    c: Distance(g3,g3) = 24
    c: Distance(g0,g0) = 27
    c: Tangent(g0,g15) = 1.5708
    c: Tangent(g8,g15) = 1.5708
    c: Tangent(g0,g16) = 1.5708
    c: Tangent(g16,g17) = 1.5708
    c: Coincident(g17,g11)
    c: Parallel(g0,g17)
    c: Radius(g15) = 1.35
    c: Coincident(g18,g7)
    c: Coincident(g18,g8)
    c: Coincident(g19,g11)
    c: Coincident(g19,g11)
    c: PointOnObject(g8,g18)
    c: PointOnObject(g11,g19)
    c: Distance(g11,g8) = 4.5
    c: Coincident(g20,g8)
    c: Coincident(g20,g0)
    c: Coincident(g21,g0)
    c: Coincident(g21,g16)
    c: Parallel(g17,g12)
    c: Equal(g15,g1)
FEATURE [PartDesign::Pad] Pad028
  Direction = (0.707107,-0.707107,1e-16)
  Length = 34
  Length2 = 10
  Midplane = true
  Placement = pos=(0,0,0) rot=(1,0,0;1.5708rad)
  Profile = -> Sketch056
  ReferenceAxis = -> Sketch056 [N_Axis]
  Refine = true
  Suppressed = false
  Type = 0
FEATURE [PartDesign::Pocket] Pocket010
  BaseFeature = -> Pad028
  Direction = (-0.707107,0.707107,-1e-16)
  Length = 24
  Length2 = 5
  Midplane = true
  Placement = pos=(0,0,0) rot=(1,0,0;1.5708rad)
  Profile = -> Sketch056
  ReferenceAxis = -> Sketch056 [N_Axis]
  Refine = true
  Suppressed = false
  Type = 0
FEATURE [PartDesign::PolarPattern] PolarPattern005
  Angle = 360
  Axis = -> Z_Axis018
  Mode = 0
  Occurrences = 4
  Offset = 120
  Placement = pos=(0,0,0) rot=(1,0,0;1.5708rad)
  Refine = true
  Suppressed = false
  TransformMode = 0
FEATURE [PartDesign::MultiTransform] MultiTransform002
  BaseFeature = -> Pocket010
  Originals = -> [Pad028,Pocket010]
  Placement = pos=(0,0,0) rot=(1,0,0;1.5708rad)
  Refine = true
  Suppressed = false
  TransformMode = 0
  Transformations = -> [PolarPattern005]
FEATURE [PartDesign::Body] Body018  label="Displaybrackets"
  AllowCompound = true
  Group = -> [Sketch056,Pad028,Pocket010,MultiTransform002,PolarPattern005]
  Origin = -> Origin018
  Tip = -> MultiTransform002
COMPONENT P9 — recipe-attached ("Displaybrackets_cut", modeled in this document).
Construction recipe (the document's own serialized feature program — sketch geometry with constraints, then the solid features built on it; lengths are millimeters unless a unit is written):

FEATURE [PartDesign::SubShapeBinder] Binder035
  BindCopyOnChange = 0
  BindMode = 0
  ClaimChildren = false
  Context = -> Body019 [Binder035.]
  Fuse = false
  MakeFace = true
  Offset = 0.1
  OffsetFill = false
  OffsetIntersection = false
  OffsetJoinType = 0
  OffsetOpenResult = false
  PartialLoad = false
  Refine = true
  Relative = true
  Support = -> [Body018[Sketch056.]]
  _Version = 2
FEATURE [PartDesign::Pad] Pad029
  Direction = (-0.707107,0.707107,0)
  Length = 34.6
  Length2 = 10
  Midplane = true
  Profile = -> Binder035
  Refine = true
  Suppressed = false
  Type = 0
FEATURE [PartDesign::Pocket] Pocket011
  BaseFeature = -> Pad029
  Direction = (0.707107,-0.707107,0)
  Length = 23.4
  Length2 = 5
  Midplane = true
  Profile = -> Binder035
  Refine = true
  Suppressed = false
  Type = 0
FEATURE [PartDesign::PolarPattern] PolarPattern006
  Angle = 360
  Axis = -> Z_Axis019
  Mode = 0
  Occurrences = 4
  Offset = 120
  Refine = true
  Suppressed = false
  TransformMode = 0
FEATURE [PartDesign::MultiTransform] MultiTransform003
  BaseFeature = -> Pocket011
  Refine = true
  Suppressed = false
  TransformMode = 1
  Transformations = -> [PolarPattern006]
FEATURE [PartDesign::Body] Body019  label="Displaybrackets_cut"
  AllowCompound = true
  Group = -> [Binder035,Pad029,Pocket011,MultiTransform003,PolarPattern006]
  Origin = -> Origin019
  Tip = -> MultiTransform003
COMPONENT P10 — recipe-attached ("Pattern_cut_small", modeled in this document).
Construction recipe (the document's own serialized feature program — sketch geometry with constraints, then the solid features built on it; lengths are millimeters unless a unit is written):

FEATURE [Sketcher::SketchObject] Sketch070  label="SketchPatternXZ004"
  ArcFitTolerance = 1e-06
  AttachmentSupport = -> [XZ_Plane023]
  FullyConstrained = true
  MakeInternals = false
  MapMode = 5
  Placement = pos=(0,0,0) rot=(1,0,0;1.5708rad)
  sketch-geometry (11):
    g0: LineSegment StartX=95.8447 StartY=-2 StartZ=0 EndX=84.2977 EndY=18 EndZ=0
    g1: LineSegment [constr] StartX=84.2977 StartY=18 StartZ=0 EndX=85.6077 EndY=18 EndZ=0
    g2: LineSegment StartX=85.6077 StartY=18 StartZ=0 EndX=97.1547 EndY=-2 EndZ=0
    g3: LineSegment StartX=84.2977 StartY=18 StartZ=0 EndX=85.6077 EndY=18.7563 EndZ=0
    g4: LineSegment StartX=85.6077 StartY=18.7563 StartZ=0 EndX=85.6077 EndY=18 EndZ=0
    g5: LineSegment StartX=66.6654 StartY=48.54 StartZ=0 EndX=78.2124 EndY=28.54 EndZ=0
    g6: LineSegment StartX=78.2124 StartY=28.54 StartZ=0 EndX=79.5224 EndY=28.54 EndZ=0
    g7: LineSegment StartX=79.5224 StartY=28.54 StartZ=0 EndX=67.9754 EndY=48.54 EndZ=0
    g8: LineSegment StartX=95.8447 StartY=-2 StartZ=0 EndX=97.1547 EndY=-2 EndZ=0
    g9: LineSegment [constr] StartX=0 StartY=0 StartZ=0 EndX=96 EndY=0 EndZ=0
    g10: LineSegment StartX=66.6654 StartY=48.54 StartZ=0 EndX=67.9754 EndY=48.54 EndZ=0
  constraints (31):
    c: Coincident(g0,g1)
    c: Coincident(g1,g2)
    c: Parallel(g0,g2)
    c: Angle(g0,g-1) = 1.0472
    c: Horizontal(g1)
    c: DistanceY(g0) = 18
    c: Coincident(g4,g3)
    c: Coincident(g4,g1)
    c: Vertical(g4)
    c: Coincident(g6,g5)
    c: Coincident(g7,g6)
    c: Horizontal(g6)
    c: Tangent(g7,g2)
    c: Equal(g1,g6)
    c: Equal(g0,g5)
    c: Parallel(g5,g7)
    c: Coincident(g8,g0)
    c: Coincident(g2,g8)
    c: Horizontal(g8)
    c: DistanceX(g8,g8) = 1.31
    c: Coincident(g9,g-1)
    c: PointOnObject(g9,g-1)
    c: DistanceX(g9,g9) = 96
    c: DistanceY(g0,g9) = 2
    c: Coincident(g10,g5)
    c: Coincident(g10,g7)
    c: Horizontal(g10)
    c: DistanceY(g5) = 48.54
    c: PointOnObject(g9,g2)
    c: Coincident(g3,g0)
    c: Perpendicular(g0,g3)
FEATURE [Sketcher::SketchObject] Sketch082
  ArcFitTolerance = 1e-06
  AttachmentSupport = -> [XZ_Plane023]
  FullyConstrained = false
  MakeInternals = false
  MapMode = 5
  Placement = pos=(0,0,0) rot=(1,0,0;1.5708rad)
  sketch-geometry (8):
    g0: LineSegment StartX=71.1806 StartY=47.5387 StartZ=0 EndX=55.3726 EndY=47.5387 EndZ=0
    g1: LineSegment StartX=55.3726 StartY=47.5387 StartZ=0 EndX=55.3726 EndY=52.9897 EndZ=0
    g2: LineSegment StartX=55.3726 StartY=52.9897 StartZ=0 EndX=78.8121 EndY=52.9897 EndZ=0
    g3: LineSegment StartX=78.8121 StartY=52.9897 StartZ=0 EndX=111.518 EndY=0 EndZ=0
    g4: LineSegment StartX=111.518 StartY=0 StartZ=0 EndX=92.576 EndY=-7.517 EndZ=0
    g5: LineSegment StartX=92.576 StartY=-7.517 StartZ=0 EndX=92.1961 EndY=-0.945236 EndZ=0
    g6: LineSegment StartX=92.1961 StartY=-0.945236 StartZ=0 EndX=98.3119 EndY=-0.945236 EndZ=0
    g7: LineSegment StartX=98.3119 StartY=-0.945236 StartZ=0 EndX=71.1806 EndY=47.5387 EndZ=0
  constraints (12):
    c: Horizontal(g0)
    c: Coincident(g0,g1)
    c: Vertical(g1)
    c: Coincident(g1,g2)
    c: Horizontal(g2)
    c: Coincident(g2,g3)
    c: Coincident(g3,g4)
    c: Coincident(g4,g5)
    c: Coincident(g5,g6)
    c: Horizontal(g6)
    c: Coincident(g6,g7)
    c: Coincident(g7,g0)
FEATURE [PartDesign::Revolution] Revolution010
  Angle = 360
  Angle2 = 60
  Axis = (0,2e-16,1)
  Base = (0,0,0)
  Placement = pos=(0,0,0) rot=(1,0,0;1.5708rad)
  Profile = -> Sketch082
  ReferenceAxis = -> Sketch082 [V_Axis]
  Refine = true
  Reversed = true
  Suppressed = false
  Type = 0
FEATURE [PartDesign::Revolution] Revolution007
  Angle = 2.25
  Angle2 = 60
  Axis = (0,2e-16,1)
  Base = (0,0,0)
  BaseFeature = -> Revolution010
  Midplane = true
  Placement = pos=(0,0,0) rot=(1,0,0;1.5708rad)
  Profile = -> Sketch070
  ReferenceAxis = -> Sketch070 [V_Axis]
  Refine = true
  Reversed = true
  Suppressed = false
  Type = 0
FEATURE [PartDesign::PolarPattern] PolarPattern013
  Angle = 360
  Axis = -> Z_Axis023
  BaseFeature = -> Revolution007
  Mode = 0
  Occurrences = 8
  Offset = 120
  Originals = -> [Revolution007]
  Placement = pos=(0,0,0) rot=(1,0,0;1.5708rad)
  Refine = true
  Suppressed = false
  TransformMode = 0
FEATURE [Sketcher::SketchObject] Sketch084  label="SketchPatternXZ005"
  ArcFitTolerance = 1e-06
  AttachmentSupport = -> [XZ_Plane023]
  FullyConstrained = true
  MakeInternals = false
  MapMode = 5
  Placement = pos=(0,0,0) rot=(1,0,0;1.5708rad)
  sketch-geometry (10):
    g0: LineSegment StartX=95.8497 StartY=-2 StartZ=0 EndX=88.3441 EndY=11 EndZ=0
    g1: LineSegment StartX=89.6491 StartY=11 StartZ=0 EndX=97.1547 EndY=-2 EndZ=0
    g2: LineSegment StartX=66.6704 StartY=48.54 StartZ=0 EndX=74.176 EndY=35.54 EndZ=0
    g3: LineSegment StartX=74.176 StartY=35.54 StartZ=0 EndX=75.481 EndY=35.54 EndZ=0
    g4: LineSegment StartX=75.481 StartY=35.54 StartZ=0 EndX=67.9754 EndY=48.54 EndZ=0
    g5: LineSegment StartX=95.8497 StartY=-2 StartZ=0 EndX=97.1547 EndY=-2 EndZ=0
    g6: LineSegment [constr] StartX=0 StartY=0 StartZ=0 EndX=96 EndY=0 EndZ=0
    g7: LineSegment StartX=66.6704 StartY=48.54 StartZ=0 EndX=67.9754 EndY=48.54 EndZ=0
    g8: LineSegment StartX=88.3441 StartY=11 StartZ=0 EndX=89.6491 EndY=11.7534 EndZ=0
    g9: LineSegment StartX=89.6491 StartY=11.7534 StartZ=0 EndX=89.6491 EndY=11 EndZ=0
  constraints (29):
    c: Parallel(g0,g1)
    c: Angle(g0,g-1) = 1.0472
    c: DistanceY(g0) = 11
    c: Coincident(g3,g2)
    c: Coincident(g4,g3)
    c: Horizontal(g3)
    c: Tangent(g4,g1)
    c: Equal(g0,g2)
    c: Parallel(g2,g4)
    c: Coincident(g5,g0)
    c: Coincident(g1,g5)
    c: Horizontal(g5)
    c: DistanceX(g5,g5) = 1.305
    c: Coincident(g6,g-1)
    c: PointOnObject(g6,g-1)
    c: DistanceX(g6,g6) = 96
    c: DistanceY(g0,g6) = 2
    c: Coincident(g7,g2)
    c: Coincident(g7,g4)
    c: Horizontal(g7)
    c: DistanceY(g2) = 48.54
    c: PointOnObject(g6,g1)
    c: Coincident(g0,g8)
    c: Coincident(g8,g9)
    c: Coincident(g9,g1)
    c: Vertical(g9)
    c: Perpendicular(g0,g8)
    c: Horizontal(g1,g0)
    c: Equal(g3,g5)
FEATURE [PartDesign::Revolution] Revolution008
  Angle = 2.25
  Angle2 = 60
  Axis = (0,2e-16,1)
  Base = (0,0,0)
  BaseFeature = -> PolarPattern013
  Midplane = true
  Placement = pos=(0,0,0) rot=(1,0,0;1.5708rad)
  Profile = -> Sketch084
  ReferenceAxis = -> Sketch084 [V_Axis]
  Refine = true
  Reversed = true
  Suppressed = false
  Type = 0
FEATURE [PartDesign::PolarPattern] PolarPattern014
  Angle = 360
  Axis = -> Z_Axis023
  BaseFeature = -> Revolution008
  Mode = 0
  Occurrences = 16
  Offset = 60
  Originals = -> [Revolution008]
  Placement = pos=(0,0,0) rot=(1,0,0;1.5708rad)
  Refine = true
  Suppressed = false
  TransformMode = 0
FEATURE [Sketcher::SketchObject] Sketch085  label="SketchPatternXZ006"
  ArcFitTolerance = 1e-06
  AttachmentSupport = -> [XZ_Plane023]
  FullyConstrained = true
  MakeInternals = false
  MapMode = 5
  Placement = pos=(0,0,0) rot=(1,0,0;1.5708rad)
  sketch-geometry (11):
    g0: LineSegment StartX=95.8547 StartY=-2 StartZ=0 EndX=92.1019 EndY=4.5 EndZ=0
    g1: LineSegment [constr] StartX=92.1019 StartY=4.5 StartZ=0 EndX=93.4019 EndY=4.5 EndZ=0
    g2: LineSegment StartX=93.4019 StartY=4.5 StartZ=0 EndX=97.1547 EndY=-2 EndZ=0
    g3: LineSegment StartX=92.1019 StartY=4.5 StartZ=0 EndX=93.4019 EndY=5.25056 EndZ=0
    g4: LineSegment StartX=93.4019 StartY=5.25056 StartZ=0 EndX=93.4019 EndY=4.5 EndZ=0
    g5: LineSegment StartX=66.6754 StartY=48.54 StartZ=0 EndX=70.4282 EndY=42.04 EndZ=0
    g6: LineSegment StartX=70.4282 StartY=42.04 StartZ=0 EndX=71.7282 EndY=42.04 EndZ=0
    g7: LineSegment StartX=71.7282 StartY=42.04 StartZ=0 EndX=67.9754 EndY=48.54 EndZ=0
    g8: LineSegment StartX=95.8547 StartY=-2 StartZ=0 EndX=97.1547 EndY=-2 EndZ=0
    g9: LineSegment [constr] StartX=0 StartY=0 StartZ=0 EndX=96 EndY=0 EndZ=0
    g10: LineSegment StartX=66.6754 StartY=48.54 StartZ=0 EndX=67.9754 EndY=48.54 EndZ=0
  constraints (31):
    c: Coincident(g0,g1)
    c: Coincident(g1,g2)
    c: Parallel(g0,g2)
    c: Angle(g0,g-1) = 1.0472
    c: Horizontal(g1)
    c: DistanceY(g0) = 4.5
    c: Coincident(g4,g3)
    c: Coincident(g4,g1)
    c: Vertical(g4)
    c: Coincident(g6,g5)
    c: Coincident(g7,g6)
    c: Horizontal(g6)
    c: Tangent(g7,g2)
    c: Equal(g1,g6)
    c: Equal(g0,g5)
    c: Parallel(g5,g7)
    c: Coincident(g8,g0)
    c: Coincident(g2,g8)
    c: Horizontal(g8)
    c: DistanceX(g8,g8) = 1.3
    c: Coincident(g9,g-1)
    c: PointOnObject(g9,g-1)
    c: DistanceX(g9,g9) = 96
    c: DistanceY(g0,g9) = 2
    c: Coincident(g10,g5)
    c: Coincident(g10,g7)
    c: Horizontal(g10)
    c: DistanceY(g5) = 48.54
    c: PointOnObject(g9,g2)
    c: Coincident(g3,g0)
    c: Perpendicular(g0,g3)
FEATURE [PartDesign::Revolution] Revolution009
  Angle = 2.25
  Angle2 = 60
  Axis = (0,2e-16,1)
  Base = (0,0,0)
  BaseFeature = -> PolarPattern014
  Midplane = true
  Placement = pos=(0,0,0) rot=(1,0,0;1.5708rad)
  Profile = -> Sketch085
  ReferenceAxis = -> Sketch085 [V_Axis]
  Refine = true
  Reversed = true
  Suppressed = false
  Type = 0
FEATURE [PartDesign::PolarPattern] PolarPattern015
  Angle = 360
  Axis = -> Z_Axis023
  BaseFeature = -> Revolution009
  Mode = 0
  Occurrences = 80
  Offset = 6
  Originals = -> [Revolution009]
  Placement = pos=(0,0,0) rot=(1,0,0;1.5708rad)
  Refine = true
  Suppressed = false
  TransformMode = 0
FEATURE [PartDesign::Body] Body023  label="Pattern_cut_small"
  AllowCompound = false
  Group = -> [Revolution010,Sketch070,Revolution007,PolarPattern013,Revolution008,PolarPattern014,Revolution009,PolarPattern015,Sketch082,Sketch084,Sketch085]
  Origin = -> Origin023
  Placement = pos=(0,0,0) rot=(0,0,1;1.96349rad)
  Tip = -> PolarPattern015
COMPONENT P11 — recipe-attached ("CableHolders", modeled in this document).
Construction recipe (the document's own serialized feature program — sketch geometry with constraints, then the solid features built on it; lengths are millimeters unless a unit is written):

FEATURE [Sketcher::SketchObject] Sketch087
  ArcFitTolerance = 1e-06
  AttachmentSupport = -> [XY_Plane025]
  FullyConstrained = false
  MakeInternals = false
  MapMode = 5
  sketch-geometry (20):
    g0: LineSegment StartX=-22.5994 StartY=-35.3126 StartZ=0 EndX=-22.5994 EndY=-66.5973 EndZ=0
    g1: ArcOfCircle CenterX=-25.5994 CenterY=-66.5973 CenterZ=0 NormalX=0 NormalY=0 NormalZ=1 AngleXU=0 Radius=3 StartAngle=3.14159 EndAngle=6.28319
    g2: LineSegment StartX=-28.5994 StartY=-66.5973 StartZ=0 EndX=-28.5994 EndY=-35.3126 EndZ=0
    g3: LineSegment StartX=-28.5994 StartY=-35.3126 StartZ=0 EndX=-22.5994 EndY=-35.3126 EndZ=0
    g4: LineSegment StartX=83.7079 StartY=-28.7165 StartZ=0 EndX=65.1633 EndY=-21.5713 EndZ=0
    g5: ArcOfCircle CenterX=64.0847 CenterY=-24.3707 CenterZ=0 NormalX=0 NormalY=0 NormalZ=1 AngleXU=0 Radius=3 StartAngle=1.20303 EndAngle=4.34462
    g6: LineSegment StartX=63.0061 StartY=-27.1701 StartZ=0 EndX=81.5507 EndY=-34.3153 EndZ=0
    g7: LineSegment StartX=81.5507 StartY=-34.3153 StartZ=0 EndX=83.7079 EndY=-28.7165 EndZ=0
    g8: LineSegment StartX=-88.6952 StartY=3.43156 StartZ=0 EndX=-69.305 EndY=3.43156 EndZ=0
    g9: ArcOfCircle CenterX=-69.305 CenterY=0 CenterZ=0 NormalX=0 NormalY=0 NormalZ=1 AngleXU=0 Radius=3.43156 StartAngle=4.71239 EndAngle=7.85398
    g10: LineSegment StartX=-69.305 StartY=-3.43156 StartZ=0 EndX=-88.6952 EndY=-3.43156 EndZ=0
    g11: LineSegment StartX=-88.6952 StartY=-3.43156 StartZ=0 EndX=-88.6952 EndY=3.43156 EndZ=0
    g12: LineSegment StartX=22.5994 StartY=-35.3126 StartZ=0 EndX=22.5994 EndY=-66.5973 EndZ=0
    g13: ArcOfCircle CenterX=25.5994 CenterY=-66.5973 CenterZ=0 NormalX=0 NormalY=0 NormalZ=1 AngleXU=0 Radius=3 StartAngle=3.14159 EndAngle=6.28319
    g14: LineSegment StartX=28.5994 StartY=-66.5973 StartZ=0 EndX=28.5994 EndY=-35.3126 EndZ=0
    g15: LineSegment StartX=28.5994 StartY=-35.3126 StartZ=0 EndX=22.5994 EndY=-35.3126 EndZ=0
    g16: LineSegment StartX=83.7079 StartY=28.7165 StartZ=0 EndX=65.1633 EndY=21.5713 EndZ=0
    g17: ArcOfCircle CenterX=64.0847 CenterY=24.3707 CenterZ=0 NormalX=0 NormalY=0 NormalZ=1 AngleXU=0 Radius=3 StartAngle=1.93857 EndAngle=5.08016
    g18: LineSegment StartX=63.0061 StartY=27.1701 StartZ=0 EndX=81.5507 EndY=34.3153 EndZ=0
    g19: LineSegment StartX=81.5507 StartY=34.3153 StartZ=0 EndX=83.7079 EndY=28.7165 EndZ=0
  constraints (38):
    c: Vertical(g0)
    c: Tangent(g0,g1) = 1.5708
    c: Tangent(g1,g2) = 1.5708
    c: Coincident(g2,g3)
    c: Coincident(g3,g0)
    c: Horizontal(g3)
    c: Vertical(g2)
    c: Radius(g1) = 3
    c: Tangent(g4,g5) = -1.5708
    c: Tangent(g5,g6) = -1.5708
    c: Coincident(g6,g7)
    c: Coincident(g7,g4)
    c: Radius(g5) = 3
    c: Parallel(g4,g6)
    c: Perpendicular(g6,g7)
    c: Horizontal(g8)
    c: Tangent(g8,g9) = 1.5708
    c: Tangent(g9,g10) = 1.5708
    c: Coincident(g10,g11)
    c: Coincident(g11,g8)
    c: Vertical(g11)
    c: Parallel(g10,g8)
    c: PointOnObject(g9,g-1)
    c: Vertical(g12)
    c: Tangent(g12,g13) = -1.5708
    c: Tangent(g13,g14) = -1.5708
    c: Coincident(g14,g15)
    c: Coincident(g15,g12)
    c: Horizontal(g15)
    c: Vertical(g14)
    c: Radius(g13) = 3
    c: Tangent(g16,g17) = 1.5708
    c: Tangent(g17,g18) = 1.5708
    c: Coincident(g18,g19)
    c: Coincident(g19,g16)
    c: Radius(g17) = 3
    c: Parallel(g16,g18)
    c: Perpendicular(g18,g19)
FEATURE [PartDesign::Pad] Pad033
  Direction = (0,0,1)
  Length = 2
  Length2 = 10
  Profile = -> Sketch087
  ReferenceAxis = -> Sketch087 [N_Axis]
  Refine = true
  Suppressed = false
  Type = 0
FEATURE [PartDesign::Body] Body025  label="CableHolders"
  AllowCompound = true
  Group = -> [Sketch087,Pad033]
  Origin = -> Origin025
  Tip = -> Pad033
